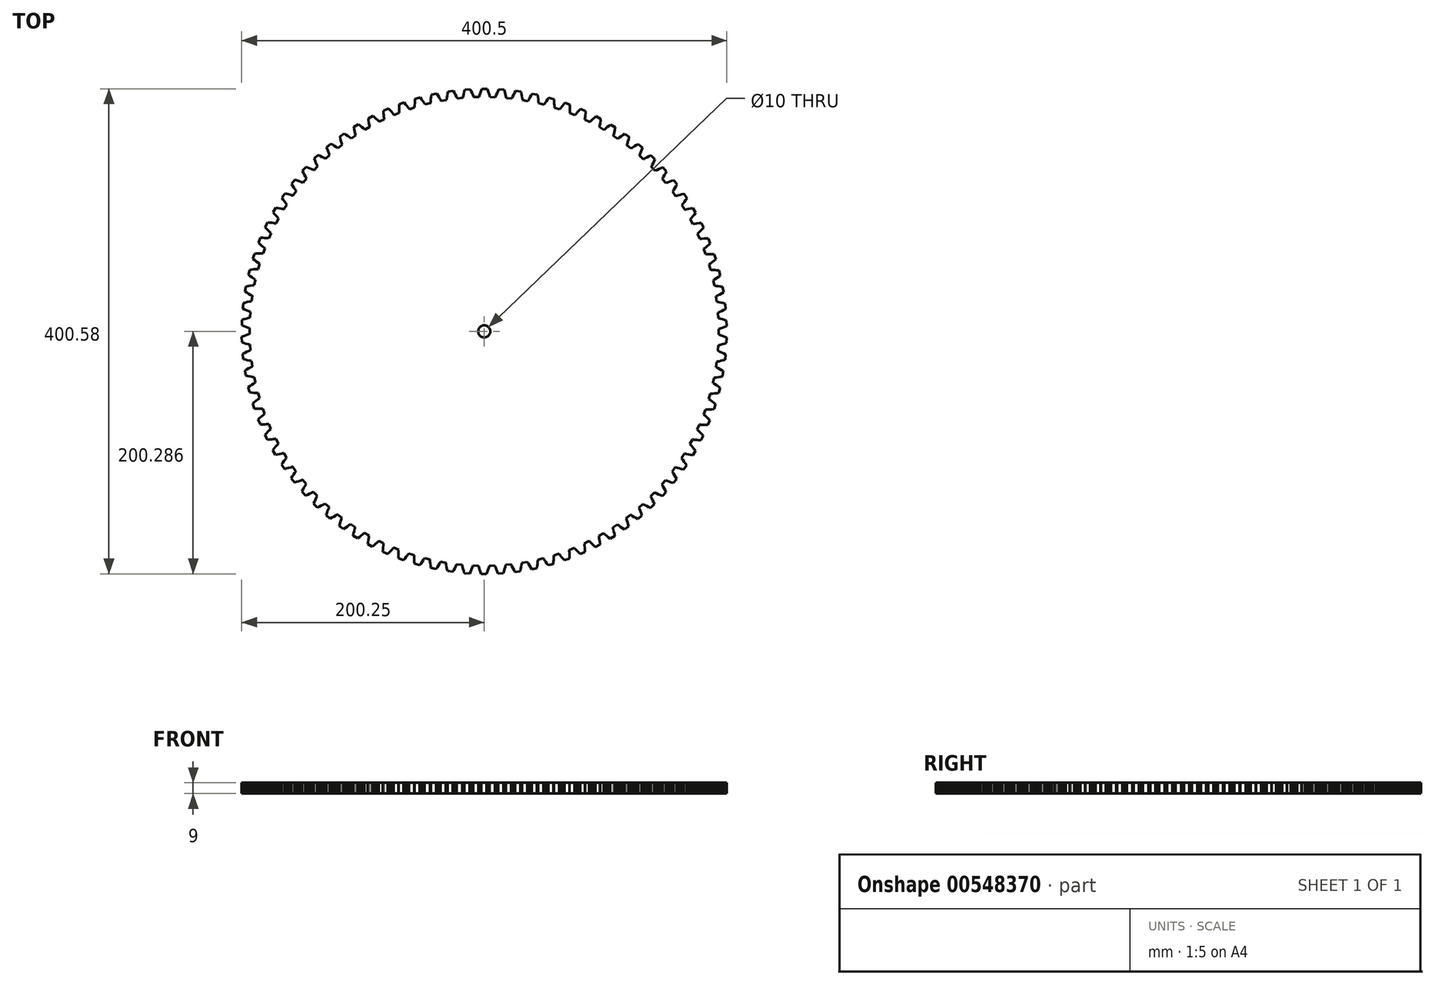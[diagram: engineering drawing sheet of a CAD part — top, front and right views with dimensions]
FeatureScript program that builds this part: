
annotation { "Feature Type Name" : "Feature", "Feature Type Description" : "" }
export const myFeature = defineFeature(function(context is Context, id is Id, definition is map)
    precondition{}
    {
        {
            var Q0;
            Q0=qCreatedBy(makeId("Top.planeOp"),FACE);
            var sketch = newSketch(context, id + "F0", { "sketchPlane" : qUnion([Q0])});
            skLineSegment(sketch, "E0.0.0", {"start": v(83.63, 88.8) * mm, "end": v(83.62, 84.25) * mm});
            skLineSegment(sketch, "E0.0.1", {"start": v(83.62, 84.25) * mm, "end": v(84.03, 84.11) * mm});
            skLineSegment(sketch, "E0.0.2", {"start": v(84.03, 84.11) * mm, "end": v(84.44, 83.97) * mm});
            skLineSegment(sketch, "E0.0.3", {"start": v(84.44, 83.97) * mm, "end": v(85.27, 83.69) * mm});
            skLineSegment(sketch, "E0.0.4", {"start": v(85.27, 83.69) * mm, "end": v(86.9, 83.08) * mm});
            skLineSegment(sketch, "E0.0.5", {"start": v(86.9, 83.08) * mm, "end": v(88.54, 82.43) * mm});
            skLineSegment(sketch, "E0.0.6", {"start": v(88.54, 82.43) * mm, "end": v(90.18, 81.73) * mm});
            skLineSegment(sketch, "E0.0.7", {"start": v(90.18, 81.73) * mm, "end": v(90.02, 77.33) * mm});
            skLineSegment(sketch, "E0.0.8", {"start": v(90.02, 77.33) * mm, "end": v(88.34, 76.75) * mm});
            skLineSegment(sketch, "E0.0.9", {"start": v(88.34, 76.75) * mm, "end": v(86.66, 76.21) * mm});
            skLineSegment(sketch, "E0.0.10", {"start": v(86.66, 76.21) * mm, "end": v(84.98, 75.72) * mm});
            skLineSegment(sketch, "E0.0.11", {"start": v(84.98, 75.72) * mm, "end": v(84.14, 75.5) * mm});
            skLineSegment(sketch, "E0.0.12", {"start": v(84.14, 75.5) * mm, "end": v(83.72, 75.4) * mm});
            skLineSegment(sketch, "E0.0.13", {"start": v(83.72, 75.4) * mm, "end": v(83.3, 75.29) * mm});
            skLineSegment(sketch, "E0.0.14", {"start": v(83.3, 75.29) * mm, "end": v(82.97, 70.74) * mm});
            skLineSegment(sketch, "E0.0.15", {"start": v(82.97, 70.74) * mm, "end": v(83.37, 70.58) * mm});
            skLineSegment(sketch, "E0.0.16", {"start": v(83.37, 70.58) * mm, "end": v(83.77, 70.41) * mm});
            skLineSegment(sketch, "E0.0.17", {"start": v(83.77, 70.41) * mm, "end": v(84.57, 70.07) * mm});
            skLineSegment(sketch, "E0.0.18", {"start": v(84.57, 70.07) * mm, "end": v(86.17, 69.35) * mm});
            skLineSegment(sketch, "E0.0.19", {"start": v(86.17, 69.35) * mm, "end": v(87.75, 68.58) * mm});
            skLineSegment(sketch, "E0.0.20", {"start": v(87.75, 68.58) * mm, "end": v(89.33, 67.77) * mm});
            skLineSegment(sketch, "E0.0.21", {"start": v(89.33, 67.77) * mm, "end": v(88.87, 63.4) * mm});
            skLineSegment(sketch, "E0.0.22", {"start": v(88.87, 63.4) * mm, "end": v(87.15, 62.93) * mm});
            skLineSegment(sketch, "E0.0.23", {"start": v(87.15, 62.93) * mm, "end": v(85.44, 62.51) * mm});
            skLineSegment(sketch, "E0.0.24", {"start": v(85.44, 62.51) * mm, "end": v(83.73, 62.15) * mm});
            skLineSegment(sketch, "E0.0.25", {"start": v(83.73, 62.15) * mm, "end": v(82.88, 61.98) * mm});
            skLineSegment(sketch, "E0.0.26", {"start": v(82.88, 61.98) * mm, "end": v(82.45, 61.9) * mm});
            skLineSegment(sketch, "E0.0.27", {"start": v(82.45, 61.9) * mm, "end": v(82.02, 61.83) * mm});
            skLineSegment(sketch, "E0.0.28", {"start": v(82.02, 61.83) * mm, "end": v(81.38, 57.31) * mm});
            skLineSegment(sketch, "E0.0.29", {"start": v(81.38, 57.31) * mm, "end": v(81.77, 57.12) * mm});
            skLineSegment(sketch, "E0.0.30", {"start": v(81.77, 57.12) * mm, "end": v(82.16, 56.93) * mm});
            skLineSegment(sketch, "E0.0.31", {"start": v(82.16, 56.93) * mm, "end": v(82.93, 56.54) * mm});
            skLineSegment(sketch, "E0.0.32", {"start": v(82.93, 56.54) * mm, "end": v(84.47, 55.7) * mm});
            skLineSegment(sketch, "E0.0.33", {"start": v(84.47, 55.7) * mm, "end": v(86, 54.83) * mm});
            skLineSegment(sketch, "E0.0.34", {"start": v(86, 54.83) * mm, "end": v(87.52, 53.9) * mm});
            skLineSegment(sketch, "E0.0.35", {"start": v(87.52, 53.9) * mm, "end": v(86.75, 49.57) * mm});
            skLineSegment(sketch, "E0.0.36", {"start": v(86.75, 49.57) * mm, "end": v(85, 49.23) * mm});
            skLineSegment(sketch, "E0.0.37", {"start": v(85, 49.23) * mm, "end": v(83.27, 48.94) * mm});
            skLineSegment(sketch, "E0.0.38", {"start": v(83.27, 48.94) * mm, "end": v(81.54, 48.69) * mm});
            skLineSegment(sketch, "E0.0.39", {"start": v(81.54, 48.69) * mm, "end": v(80.68, 48.58) * mm});
            skLineSegment(sketch, "E0.0.40", {"start": v(80.68, 48.58) * mm, "end": v(80.24, 48.53) * mm});
            skLineSegment(sketch, "E0.0.41", {"start": v(80.24, 48.53) * mm, "end": v(79.82, 48.5) * mm});
            skLineSegment(sketch, "E0.0.42", {"start": v(79.82, 48.5) * mm, "end": v(78.86, 44.03) * mm});
            skLineSegment(sketch, "E0.0.43", {"start": v(78.86, 44.03) * mm, "end": v(79.23, 43.82) * mm});
            skLineSegment(sketch, "E0.0.44", {"start": v(79.23, 43.82) * mm, "end": v(79.6, 43.6) * mm});
            skLineSegment(sketch, "E0.0.45", {"start": v(79.6, 43.6) * mm, "end": v(80.35, 43.15) * mm});
            skLineSegment(sketch, "E0.0.46", {"start": v(80.35, 43.15) * mm, "end": v(81.83, 42.21) * mm});
            skLineSegment(sketch, "E0.0.47", {"start": v(81.83, 42.21) * mm, "end": v(83.3, 41.23) * mm});
            skLineSegment(sketch, "E0.0.48", {"start": v(83.3, 41.23) * mm, "end": v(84.75, 40.2) * mm});
            skLineSegment(sketch, "E0.0.49", {"start": v(84.75, 40.2) * mm, "end": v(83.67, 35.93) * mm});
            skLineSegment(sketch, "E0.0.50", {"start": v(83.67, 35.93) * mm, "end": v(81.91, 35.72) * mm});
            skLineSegment(sketch, "E0.0.51", {"start": v(81.91, 35.72) * mm, "end": v(80.16, 35.54) * mm});
            skLineSegment(sketch, "E0.0.52", {"start": v(80.16, 35.54) * mm, "end": v(78.41, 35.42) * mm});
            skLineSegment(sketch, "E0.0.53", {"start": v(78.41, 35.42) * mm, "end": v(77.54, 35.37) * mm});
            skLineSegment(sketch, "E0.0.54", {"start": v(77.54, 35.37) * mm, "end": v(77.11, 35.35) * mm});
            skLineSegment(sketch, "E0.0.55", {"start": v(77.11, 35.35) * mm, "end": v(76.68, 35.34) * mm});
            skLineSegment(sketch, "E0.0.56", {"start": v(76.68, 35.34) * mm, "end": v(75.42, 30.96) * mm});
            skLineSegment(sketch, "E0.0.57", {"start": v(75.42, 30.96) * mm, "end": v(75.78, 30.72) * mm});
            skLineSegment(sketch, "E0.0.58", {"start": v(75.78, 30.72) * mm, "end": v(76.13, 30.47) * mm});
            skLineSegment(sketch, "E0.0.59", {"start": v(76.13, 30.47) * mm, "end": v(76.84, 29.97) * mm});
            skLineSegment(sketch, "E0.0.60", {"start": v(76.84, 29.97) * mm, "end": v(78.25, 28.94) * mm});
            skLineSegment(sketch, "E0.0.61", {"start": v(78.25, 28.94) * mm, "end": v(79.64, 27.85) * mm});
            skLineSegment(sketch, "E0.0.62", {"start": v(79.64, 27.85) * mm, "end": v(81.02, 26.73) * mm});
            skLineSegment(sketch, "E0.0.63", {"start": v(81.02, 26.73) * mm, "end": v(79.65, 22.54) * mm});
            skLineSegment(sketch, "E0.0.64", {"start": v(79.65, 22.54) * mm, "end": v(77.88, 22.45) * mm});
            skLineSegment(sketch, "E0.0.65", {"start": v(77.88, 22.45) * mm, "end": v(76.12, 22.4) * mm});
            skLineSegment(sketch, "E0.0.66", {"start": v(76.12, 22.4) * mm, "end": v(74.37, 22.4) * mm});
            skLineSegment(sketch, "E0.0.67", {"start": v(74.37, 22.4) * mm, "end": v(73.5, 22.4) * mm});
            skLineSegment(sketch, "E0.0.68", {"start": v(73.5, 22.4) * mm, "end": v(73.07, 22.42) * mm});
            skLineSegment(sketch, "E0.0.69", {"start": v(73.07, 22.42) * mm, "end": v(72.64, 22.44) * mm});
            skLineSegment(sketch, "E0.0.70", {"start": v(72.64, 22.44) * mm, "end": v(71.07, 18.16) * mm});
            skLineSegment(sketch, "E0.0.71", {"start": v(71.07, 18.16) * mm, "end": v(71.41, 17.89) * mm});
            skLineSegment(sketch, "E0.0.72", {"start": v(71.41, 17.89) * mm, "end": v(71.75, 17.62) * mm});
            skLineSegment(sketch, "E0.0.73", {"start": v(71.75, 17.62) * mm, "end": v(72.42, 17.07) * mm});
            skLineSegment(sketch, "E0.0.74", {"start": v(72.42, 17.07) * mm, "end": v(73.76, 15.94) * mm});
            skLineSegment(sketch, "E0.0.75", {"start": v(73.76, 15.94) * mm, "end": v(75.07, 14.77) * mm});
            skLineSegment(sketch, "E0.0.76", {"start": v(75.07, 14.77) * mm, "end": v(76.37, 13.55) * mm});
            skLineSegment(sketch, "E0.0.77", {"start": v(76.37, 13.55) * mm, "end": v(74.71, 9.47) * mm});
            skLineSegment(sketch, "E0.0.78", {"start": v(74.71, 9.47) * mm, "end": v(72.93, 9.5) * mm});
            skLineSegment(sketch, "E0.0.79", {"start": v(72.93, 9.5) * mm, "end": v(71.17, 9.57) * mm});
            skLineSegment(sketch, "E0.0.80", {"start": v(71.17, 9.57) * mm, "end": v(69.43, 9.69) * mm});
            skLineSegment(sketch, "E0.0.81", {"start": v(69.43, 9.69) * mm, "end": v(68.56, 9.76) * mm});
            skLineSegment(sketch, "E0.0.82", {"start": v(68.56, 9.76) * mm, "end": v(68.13, 9.8) * mm});
            skLineSegment(sketch, "E0.0.83", {"start": v(68.13, 9.8) * mm, "end": v(67.7, 9.85) * mm});
            skLineSegment(sketch, "E0.0.84", {"start": v(67.7, 9.85) * mm, "end": v(65.84, 5.69) * mm});
            skLineSegment(sketch, "E0.0.85", {"start": v(65.84, 5.69) * mm, "end": v(66.16, 5.4) * mm});
            skLineSegment(sketch, "E0.0.86", {"start": v(66.16, 5.4) * mm, "end": v(66.48, 5.1) * mm});
            skLineSegment(sketch, "E0.0.87", {"start": v(66.48, 5.1) * mm, "end": v(67.12, 4.51) * mm});
            skLineSegment(sketch, "E0.0.88", {"start": v(67.12, 4.51) * mm, "end": v(68.37, 3.3) * mm});
            skLineSegment(sketch, "E0.0.89", {"start": v(68.37, 3.3) * mm, "end": v(69.6, 2.03) * mm});
            skLineSegment(sketch, "E0.0.90", {"start": v(69.6, 2.03) * mm, "end": v(70.8, 0.72) * mm});
            skLineSegment(sketch, "E0.0.91", {"start": v(70.8, 0.72) * mm, "end": v(68.87, -3.23) * mm});
            skLineSegment(sketch, "E0.0.92", {"start": v(68.87, -3.23) * mm, "end": v(67.1, -3.08) * mm});
            skLineSegment(sketch, "E0.0.93", {"start": v(67.1, -3.08) * mm, "end": v(65.34, -2.89) * mm});
            skLineSegment(sketch, "E0.0.94", {"start": v(65.34, -2.89) * mm, "end": v(63.61, -2.65) * mm});
            skLineSegment(sketch, "E0.0.95", {"start": v(63.61, -2.65) * mm, "end": v(62.75, -2.51) * mm});
            skLineSegment(sketch, "E0.0.96", {"start": v(62.75, -2.51) * mm, "end": v(62.33, -2.44) * mm});
            skLineSegment(sketch, "E0.0.97", {"start": v(62.33, -2.44) * mm, "end": v(61.9, -2.36) * mm});
            skLineSegment(sketch, "E0.0.98", {"start": v(61.9, -2.36) * mm, "end": v(59.76, -6.38) * mm});
            skLineSegment(sketch, "E0.0.99", {"start": v(59.76, -6.38) * mm, "end": v(60.06, -6.7) * mm});
            skLineSegment(sketch, "E0.0.100", {"start": v(60.06, -6.7) * mm, "end": v(60.35, -7.01) * mm});
            skLineSegment(sketch, "E0.0.101", {"start": v(60.35, -7.01) * mm, "end": v(60.94, -7.65) * mm});
            skLineSegment(sketch, "E0.0.102", {"start": v(60.94, -7.65) * mm, "end": v(62.1, -8.95) * mm});
            skLineSegment(sketch, "E0.0.103", {"start": v(62.1, -8.95) * mm, "end": v(63.24, -10.3) * mm});
            skLineSegment(sketch, "E0.0.104", {"start": v(63.24, -10.3) * mm, "end": v(64.36, -11.68) * mm});
            skLineSegment(sketch, "E0.0.105", {"start": v(64.36, -11.68) * mm, "end": v(62.15, -15.5) * mm});
            skLineSegment(sketch, "E0.0.106", {"start": v(62.15, -15.5) * mm, "end": v(60.4, -15.22) * mm});
            skLineSegment(sketch, "E0.0.107", {"start": v(60.4, -15.22) * mm, "end": v(58.66, -14.9) * mm});
            skLineSegment(sketch, "E0.0.108", {"start": v(58.66, -14.9) * mm, "end": v(56.95, -14.54) * mm});
            skLineSegment(sketch, "E0.0.109", {"start": v(56.95, -14.54) * mm, "end": v(56.1, -14.35) * mm});
            skLineSegment(sketch, "E0.0.110", {"start": v(56.1, -14.35) * mm, "end": v(55.68, -14.25) * mm});
            skLineSegment(sketch, "E0.0.111", {"start": v(55.68, -14.25) * mm, "end": v(55.26, -14.14) * mm});
            skLineSegment(sketch, "E0.0.112", {"start": v(55.26, -14.14) * mm, "end": v(52.84, -18) * mm});
            skLineSegment(sketch, "E0.0.113", {"start": v(52.84, -18) * mm, "end": v(53.12, -18.34) * mm});
            skLineSegment(sketch, "E0.0.114", {"start": v(53.12, -18.34) * mm, "end": v(53.4, -18.67) * mm});
            skLineSegment(sketch, "E0.0.115", {"start": v(53.4, -18.67) * mm, "end": v(53.94, -19.35) * mm});
            skLineSegment(sketch, "E0.0.116", {"start": v(53.94, -19.35) * mm, "end": v(55, -20.73) * mm});
            skLineSegment(sketch, "E0.0.117", {"start": v(55, -20.73) * mm, "end": v(56.05, -22.15) * mm});
            skLineSegment(sketch, "E0.0.118", {"start": v(56.05, -22.15) * mm, "end": v(57.06, -23.61) * mm});
            skLineSegment(sketch, "E0.0.119", {"start": v(57.06, -23.61) * mm, "end": v(54.6, -27.26) * mm});
            skLineSegment(sketch, "E0.0.120", {"start": v(54.6, -27.26) * mm, "end": v(52.86, -26.86) * mm});
            skLineSegment(sketch, "E0.0.121", {"start": v(52.86, -26.86) * mm, "end": v(51.15, -26.42) * mm});
            skLineSegment(sketch, "E0.0.122", {"start": v(51.15, -26.42) * mm, "end": v(49.47, -25.95) * mm});
            skLineSegment(sketch, "E0.0.123", {"start": v(49.47, -25.95) * mm, "end": v(48.64, -25.7) * mm});
            skLineSegment(sketch, "E0.0.124", {"start": v(48.64, -25.7) * mm, "end": v(48.23, -25.56) * mm});
            skLineSegment(sketch, "E0.0.125", {"start": v(48.23, -25.56) * mm, "end": v(47.82, -25.43) * mm});
            skLineSegment(sketch, "E0.0.126", {"start": v(47.82, -25.43) * mm, "end": v(45.13, -29.11) * mm});
            skLineSegment(sketch, "E0.0.127", {"start": v(45.13, -29.11) * mm, "end": v(45.39, -29.46) * mm});
            skLineSegment(sketch, "E0.0.128", {"start": v(45.39, -29.46) * mm, "end": v(45.64, -29.81) * mm});
            skLineSegment(sketch, "E0.0.129", {"start": v(45.64, -29.81) * mm, "end": v(46.14, -30.53) * mm});
            skLineSegment(sketch, "E0.0.130", {"start": v(46.14, -30.53) * mm, "end": v(47.1, -31.98) * mm});
            skLineSegment(sketch, "E0.0.131", {"start": v(47.1, -31.98) * mm, "end": v(48.04, -33.47) * mm});
            skLineSegment(sketch, "E0.0.132", {"start": v(48.04, -33.47) * mm, "end": v(48.95, -35) * mm});
            skLineSegment(sketch, "E0.0.133", {"start": v(48.95, -35) * mm, "end": v(46.24, -38.47) * mm});
            skLineSegment(sketch, "E0.0.134", {"start": v(46.24, -38.47) * mm, "end": v(44.54, -37.95) * mm});
            skLineSegment(sketch, "E0.0.135", {"start": v(44.54, -37.95) * mm, "end": v(42.86, -37.4) * mm});
            skLineSegment(sketch, "E0.0.136", {"start": v(42.86, -37.4) * mm, "end": v(41.22, -36.8) * mm});
            skLineSegment(sketch, "E0.0.137", {"start": v(41.22, -36.8) * mm, "end": v(40.4, -36.49) * mm});
            skLineSegment(sketch, "E0.0.138", {"start": v(40.4, -36.49) * mm, "end": v(40, -36.33) * mm});
            skLineSegment(sketch, "E0.0.139", {"start": v(40, -36.33) * mm, "end": v(39.6, -36.17) * mm});
            skLineSegment(sketch, "E0.0.140", {"start": v(39.6, -36.17) * mm, "end": v(36.67, -39.66) * mm});
            skLineSegment(sketch, "E0.0.141", {"start": v(36.67, -39.66) * mm, "end": v(36.9, -40.02) * mm});
            skLineSegment(sketch, "E0.0.142", {"start": v(36.9, -40.02) * mm, "end": v(37.13, -40.4) * mm});
            skLineSegment(sketch, "E0.0.143", {"start": v(37.13, -40.4) * mm, "end": v(37.57, -41.14) * mm});
            skLineSegment(sketch, "E0.0.144", {"start": v(37.57, -41.14) * mm, "end": v(38.44, -42.66) * mm});
            skLineSegment(sketch, "E0.0.145", {"start": v(38.44, -42.66) * mm, "end": v(39.27, -44.2) * mm});
            skLineSegment(sketch, "E0.0.146", {"start": v(39.27, -44.2) * mm, "end": v(40.07, -45.8) * mm});
            skLineSegment(sketch, "E0.0.147", {"start": v(40.07, -45.8) * mm, "end": v(37.12, -49.06) * mm});
            skLineSegment(sketch, "E0.0.148", {"start": v(37.12, -49.06) * mm, "end": v(35.46, -48.43) * mm});
            skLineSegment(sketch, "E0.0.149", {"start": v(35.46, -48.43) * mm, "end": v(33.83, -47.76) * mm});
            skLineSegment(sketch, "E0.0.150", {"start": v(33.83, -47.76) * mm, "end": v(32.23, -47.05) * mm});
            skLineSegment(sketch, "E0.0.151", {"start": v(32.23, -47.05) * mm, "end": v(31.44, -46.69) * mm});
            skLineSegment(sketch, "E0.0.152", {"start": v(31.44, -46.69) * mm, "end": v(31.05, -46.5) * mm});
            skLineSegment(sketch, "E0.0.153", {"start": v(31.05, -46.5) * mm, "end": v(30.66, -46.3) * mm});
            skLineSegment(sketch, "E0.0.154", {"start": v(30.66, -46.3) * mm, "end": v(27.5, -49.58) * mm});
            skLineSegment(sketch, "E0.0.155", {"start": v(27.5, -49.58) * mm, "end": v(27.7, -49.96) * mm});
            skLineSegment(sketch, "E0.0.156", {"start": v(27.7, -49.96) * mm, "end": v(27.9, -50.35) * mm});
            skLineSegment(sketch, "E0.0.157", {"start": v(27.9, -50.35) * mm, "end": v(28.29, -51.12) * mm});
            skLineSegment(sketch, "E0.0.158", {"start": v(28.29, -51.12) * mm, "end": v(29.05, -52.7) * mm});
            skLineSegment(sketch, "E0.0.159", {"start": v(29.05, -52.7) * mm, "end": v(29.77, -54.3) * mm});
            skLineSegment(sketch, "E0.0.160", {"start": v(29.77, -54.3) * mm, "end": v(30.46, -55.95) * mm});
            skLineSegment(sketch, "E0.0.161", {"start": v(30.46, -55.95) * mm, "end": v(27.28, -59) * mm});
            skLineSegment(sketch, "E0.0.162", {"start": v(27.28, -59) * mm, "end": v(25.67, -58.25) * mm});
            skLineSegment(sketch, "E0.0.163", {"start": v(25.67, -58.25) * mm, "end": v(24.1, -57.47) * mm});
            skLineSegment(sketch, "E0.0.164", {"start": v(24.1, -57.47) * mm, "end": v(22.55, -56.65) * mm});
            skLineSegment(sketch, "E0.0.165", {"start": v(22.55, -56.65) * mm, "end": v(21.79, -56.23) * mm});
            skLineSegment(sketch, "E0.0.166", {"start": v(21.79, -56.23) * mm, "end": v(21.41, -56.02) * mm});
            skLineSegment(sketch, "E0.0.167", {"start": v(21.41, -56.02) * mm, "end": v(21.04, -55.8) * mm});
            skLineSegment(sketch, "E0.0.168", {"start": v(21.04, -55.8) * mm, "end": v(17.64, -58.85) * mm});
            skLineSegment(sketch, "E0.0.169", {"start": v(17.64, -58.85) * mm, "end": v(17.82, -59.24) * mm});
            skLineSegment(sketch, "E0.0.170", {"start": v(17.82, -59.24) * mm, "end": v(18, -59.64) * mm});
            skLineSegment(sketch, "E0.0.171", {"start": v(18, -59.64) * mm, "end": v(18.33, -60.44) * mm});
            skLineSegment(sketch, "E0.0.172", {"start": v(18.33, -60.44) * mm, "end": v(18.98, -62.06) * mm});
            skLineSegment(sketch, "E0.0.173", {"start": v(18.98, -62.06) * mm, "end": v(19.58, -63.72) * mm});
            skLineSegment(sketch, "E0.0.174", {"start": v(19.58, -63.72) * mm, "end": v(20.16, -65.4) * mm});
            skLineSegment(sketch, "E0.0.175", {"start": v(20.16, -65.4) * mm, "end": v(16.78, -68.23) * mm});
            skLineSegment(sketch, "E0.0.176", {"start": v(16.78, -68.23) * mm, "end": v(15.22, -67.37) * mm});
            skLineSegment(sketch, "E0.0.177", {"start": v(15.22, -67.37) * mm, "end": v(13.7, -66.48) * mm});
            skLineSegment(sketch, "E0.0.178", {"start": v(13.7, -66.48) * mm, "end": v(12.22, -65.55) * mm});
            skLineSegment(sketch, "E0.0.179", {"start": v(12.22, -65.55) * mm, "end": v(11.49, -65.08) * mm});
            skLineSegment(sketch, "E0.0.180", {"start": v(11.49, -65.08) * mm, "end": v(11.13, -64.84) * mm});
            skLineSegment(sketch, "E0.0.181", {"start": v(11.13, -64.84) * mm, "end": v(10.77, -64.6) * mm});
            skLineSegment(sketch, "E0.0.182", {"start": v(10.77, -64.6) * mm, "end": v(7.17, -67.4) * mm});
            skLineSegment(sketch, "E0.0.183", {"start": v(7.17, -67.4) * mm, "end": v(7.32, -67.8) * mm});
            skLineSegment(sketch, "E0.0.184", {"start": v(7.32, -67.8) * mm, "end": v(7.47, -68.21) * mm});
            skLineSegment(sketch, "E0.0.185", {"start": v(7.47, -68.21) * mm, "end": v(7.75, -69.04) * mm});
            skLineSegment(sketch, "E0.0.186", {"start": v(7.75, -69.04) * mm, "end": v(8.28, -70.7) * mm});
            skLineSegment(sketch, "E0.0.187", {"start": v(8.28, -70.7) * mm, "end": v(8.77, -72.4) * mm});
            skLineSegment(sketch, "E0.0.188", {"start": v(8.77, -72.4) * mm, "end": v(9.22, -74.11) * mm});
            skLineSegment(sketch, "E0.0.189", {"start": v(9.22, -74.11) * mm, "end": v(5.66, -76.7) * mm});
            skLineSegment(sketch, "E0.0.190", {"start": v(5.66, -76.7) * mm, "end": v(4.16, -75.73) * mm});
            skLineSegment(sketch, "E0.0.191", {"start": v(4.16, -75.73) * mm, "end": v(2.7, -74.74) * mm});
            skLineSegment(sketch, "E0.0.192", {"start": v(2.7, -74.74) * mm, "end": v(1.3, -73.71) * mm});
            skLineSegment(sketch, "E0.0.193", {"start": v(1.3, -73.71) * mm, "end": v(0.6, -73.19) * mm});
            skLineSegment(sketch, "E0.0.194", {"start": v(0.6, -73.19) * mm, "end": v(0.26, -72.92) * mm});
            skLineSegment(sketch, "E0.0.195", {"start": v(0.26, -72.92) * mm, "end": v(-0.08, -72.66) * mm});
            skLineSegment(sketch, "E0.0.196", {"start": v(-0.08, -72.66) * mm, "end": v(-3.87, -75.2) * mm});
            skLineSegment(sketch, "E0.0.197", {"start": v(-3.87, -75.2) * mm, "end": v(-3.75, -75.62) * mm});
            skLineSegment(sketch, "E0.0.198", {"start": v(-3.75, -75.62) * mm, "end": v(-3.63, -76.03) * mm});
            skLineSegment(sketch, "E0.0.199", {"start": v(-3.63, -76.03) * mm, "end": v(-3.41, -76.87) * mm});
            skLineSegment(sketch, "E0.0.200", {"start": v(-3.41, -76.87) * mm, "end": v(-3, -78.57) * mm});
            skLineSegment(sketch, "E0.0.201", {"start": v(-3, -78.57) * mm, "end": v(-2.62, -80.3) * mm});
            skLineSegment(sketch, "E0.0.202", {"start": v(-2.62, -80.3) * mm, "end": v(-2.3, -82.04) * mm});
            skLineSegment(sketch, "E0.0.203", {"start": v(-2.3, -82.04) * mm, "end": v(-6.03, -84.37) * mm});
            skLineSegment(sketch, "E0.0.204", {"start": v(-6.03, -84.37) * mm, "end": v(-7.45, -83.3) * mm});
            skLineSegment(sketch, "E0.0.205", {"start": v(-7.45, -83.3) * mm, "end": v(-8.83, -82.2) * mm});
            skLineSegment(sketch, "E0.0.206", {"start": v(-8.83, -82.2) * mm, "end": v(-10.18, -81.09) * mm});
            skLineSegment(sketch, "E0.0.207", {"start": v(-10.18, -81.09) * mm, "end": v(-10.83, -80.52) * mm});
            skLineSegment(sketch, "E0.0.208", {"start": v(-10.83, -80.52) * mm, "end": v(-11.15, -80.23) * mm});
            skLineSegment(sketch, "E0.0.209", {"start": v(-11.15, -80.23) * mm, "end": v(-11.48, -79.94) * mm});
            skLineSegment(sketch, "E0.0.210", {"start": v(-11.48, -79.94) * mm, "end": v(-15.43, -82.21) * mm});
            skLineSegment(sketch, "E0.0.211", {"start": v(-15.43, -82.21) * mm, "end": v(-15.34, -82.64) * mm});
            skLineSegment(sketch, "E0.0.212", {"start": v(-15.34, -82.64) * mm, "end": v(-15.25, -83.06) * mm});
            skLineSegment(sketch, "E0.0.213", {"start": v(-15.25, -83.06) * mm, "end": v(-15.09, -83.91) * mm});
            skLineSegment(sketch, "E0.0.214", {"start": v(-15.09, -83.91) * mm, "end": v(-14.8, -85.64) * mm});
            skLineSegment(sketch, "E0.0.215", {"start": v(-14.8, -85.64) * mm, "end": v(-14.54, -87.38) * mm});
            skLineSegment(sketch, "E0.0.216", {"start": v(-14.54, -87.38) * mm, "end": v(-14.33, -89.15) * mm});
            skLineSegment(sketch, "E0.0.217", {"start": v(-14.33, -89.15) * mm, "end": v(-18.22, -91.2) * mm});
            skLineSegment(sketch, "E0.0.218", {"start": v(-18.22, -91.2) * mm, "end": v(-19.57, -90.04) * mm});
            skLineSegment(sketch, "E0.0.219", {"start": v(-19.57, -90.04) * mm, "end": v(-20.87, -88.86) * mm});
            skLineSegment(sketch, "E0.0.220", {"start": v(-20.87, -88.86) * mm, "end": v(-22.13, -87.65) * mm});
            skLineSegment(sketch, "E0.0.221", {"start": v(-22.13, -87.65) * mm, "end": v(-22.74, -87.03) * mm});
            skLineSegment(sketch, "E0.0.222", {"start": v(-22.74, -87.03) * mm, "end": v(-23.05, -86.72) * mm});
            skLineSegment(sketch, "E0.0.223", {"start": v(-23.05, -86.72) * mm, "end": v(-23.35, -86.41) * mm});
            skLineSegment(sketch, "E0.0.224", {"start": v(-23.35, -86.41) * mm, "end": v(-27.45, -88.4) * mm});
            skLineSegment(sketch, "E0.0.225", {"start": v(-27.45, -88.4) * mm, "end": v(-27.39, -88.83) * mm});
            skLineSegment(sketch, "E0.0.226", {"start": v(-27.39, -88.83) * mm, "end": v(-27.33, -89.26) * mm});
            skLineSegment(sketch, "E0.0.227", {"start": v(-27.33, -89.26) * mm, "end": v(-27.23, -90.12) * mm});
            skLineSegment(sketch, "E0.0.228", {"start": v(-27.23, -90.12) * mm, "end": v(-27.05, -91.86) * mm});
            skLineSegment(sketch, "E0.0.229", {"start": v(-27.05, -91.86) * mm, "end": v(-26.92, -93.62) * mm});
            skLineSegment(sketch, "E0.0.230", {"start": v(-26.92, -93.62) * mm, "end": v(-26.84, -95.4) * mm});
            skLineSegment(sketch, "E0.0.231", {"start": v(-26.84, -95.4) * mm, "end": v(-30.86, -97.18) * mm});
            skLineSegment(sketch, "E0.0.232", {"start": v(-30.86, -97.18) * mm, "end": v(-32.12, -95.93) * mm});
            skLineSegment(sketch, "E0.0.233", {"start": v(-32.12, -95.93) * mm, "end": v(-33.34, -94.65) * mm});
            skLineSegment(sketch, "E0.0.234", {"start": v(-33.34, -94.65) * mm, "end": v(-34.51, -93.36) * mm});
            skLineSegment(sketch, "E0.0.235", {"start": v(-34.51, -93.36) * mm, "end": v(-35.08, -92.7) * mm});
            skLineSegment(sketch, "E0.0.236", {"start": v(-35.08, -92.7) * mm, "end": v(-35.36, -92.37) * mm});
            skLineSegment(sketch, "E0.0.237", {"start": v(-35.36, -92.37) * mm, "end": v(-35.64, -92.04) * mm});
            skLineSegment(sketch, "E0.0.238", {"start": v(-35.64, -92.04) * mm, "end": v(-39.87, -93.74) * mm});
            skLineSegment(sketch, "E0.0.239", {"start": v(-39.87, -93.74) * mm, "end": v(-39.84, -94.17) * mm});
            skLineSegment(sketch, "E0.0.240", {"start": v(-39.84, -94.17) * mm, "end": v(-39.81, -94.6) * mm});
            skLineSegment(sketch, "E0.0.241", {"start": v(-39.81, -94.6) * mm, "end": v(-39.77, -95.47) * mm});
            skLineSegment(sketch, "E0.0.242", {"start": v(-39.77, -95.47) * mm, "end": v(-39.72, -97.22) * mm});
            skLineSegment(sketch, "E0.0.243", {"start": v(-39.72, -97.22) * mm, "end": v(-39.71, -98.98) * mm});
            skLineSegment(sketch, "E0.0.244", {"start": v(-39.71, -98.98) * mm, "end": v(-39.75, -100.76) * mm});
            skLineSegment(sketch, "E0.0.245", {"start": v(-39.75, -100.76) * mm, "end": v(-43.9, -102.26) * mm});
            skLineSegment(sketch, "E0.0.246", {"start": v(-43.9, -102.26) * mm, "end": v(-45.06, -100.92) * mm});
            skLineSegment(sketch, "E0.0.247", {"start": v(-45.06, -100.92) * mm, "end": v(-46.18, -99.56) * mm});
            skLineSegment(sketch, "E0.0.248", {"start": v(-46.18, -99.56) * mm, "end": v(-47.26, -98.19) * mm});
            skLineSegment(sketch, "E0.0.249", {"start": v(-47.26, -98.19) * mm, "end": v(-47.79, -97.5) * mm});
            skLineSegment(sketch, "E0.0.250", {"start": v(-47.79, -97.5) * mm, "end": v(-48.04, -97.14) * mm});
            skLineSegment(sketch, "E0.0.251", {"start": v(-48.04, -97.14) * mm, "end": v(-48.3, -96.8) * mm});
            skLineSegment(sketch, "E0.0.252", {"start": v(-48.3, -96.8) * mm, "end": v(-52.63, -98.2) * mm});
            skLineSegment(sketch, "E0.0.253", {"start": v(-52.63, -98.2) * mm, "end": v(-52.63, -98.63) * mm});
            skLineSegment(sketch, "E0.0.254", {"start": v(-52.63, -98.63) * mm, "end": v(-52.64, -99.06) * mm});
            skLineSegment(sketch, "E0.0.255", {"start": v(-52.64, -99.06) * mm, "end": v(-52.66, -99.93) * mm});
            skLineSegment(sketch, "E0.0.256", {"start": v(-52.66, -99.93) * mm, "end": v(-52.73, -101.68) * mm});
            skLineSegment(sketch, "E0.0.257", {"start": v(-52.73, -101.68) * mm, "end": v(-52.84, -103.44) * mm});
            skLineSegment(sketch, "E0.0.258", {"start": v(-52.84, -103.44) * mm, "end": v(-53, -105.2) * mm});
            skLineSegment(sketch, "E0.0.259", {"start": v(-53, -105.2) * mm, "end": v(-57.24, -106.41) * mm});
            skLineSegment(sketch, "E0.0.260", {"start": v(-57.24, -106.41) * mm, "end": v(-58.31, -105) * mm});
            skLineSegment(sketch, "E0.0.261", {"start": v(-58.31, -105) * mm, "end": v(-59.34, -103.56) * mm});
            skLineSegment(sketch, "E0.0.262", {"start": v(-59.34, -103.56) * mm, "end": v(-60.32, -102.12) * mm});
            skLineSegment(sketch, "E0.0.263", {"start": v(-60.32, -102.12) * mm, "end": v(-60.8, -101.39) * mm});
            skLineSegment(sketch, "E0.0.264", {"start": v(-60.8, -101.39) * mm, "end": v(-61.02, -101.02) * mm});
            skLineSegment(sketch, "E0.0.265", {"start": v(-61.02, -101.02) * mm, "end": v(-61.25, -100.66) * mm});
            skLineSegment(sketch, "E0.0.266", {"start": v(-61.25, -100.66) * mm, "end": v(-65.68, -101.75) * mm});
            skLineSegment(sketch, "E0.0.267", {"start": v(-65.68, -101.75) * mm, "end": v(-65.7, -102.18) * mm});
            skLineSegment(sketch, "E0.0.268", {"start": v(-65.7, -102.18) * mm, "end": v(-65.74, -102.61) * mm});
            skLineSegment(sketch, "E0.0.269", {"start": v(-65.74, -102.61) * mm, "end": v(-65.82, -103.48) * mm});
            skLineSegment(sketch, "E0.0.270", {"start": v(-65.82, -103.48) * mm, "end": v(-66.01, -105.22) * mm});
            skLineSegment(sketch, "E0.0.271", {"start": v(-66.01, -105.22) * mm, "end": v(-66.25, -106.96) * mm});
            skLineSegment(sketch, "E0.0.272", {"start": v(-66.25, -106.96) * mm, "end": v(-66.54, -108.72) * mm});
            skLineSegment(sketch, "E0.0.273", {"start": v(-66.54, -108.72) * mm, "end": v(-70.85, -109.63) * mm});
            skLineSegment(sketch, "E0.0.274", {"start": v(-70.85, -109.63) * mm, "end": v(-71.82, -108.14) * mm});
            skLineSegment(sketch, "E0.0.275", {"start": v(-71.82, -108.14) * mm, "end": v(-72.74, -106.64) * mm});
            skLineSegment(sketch, "E0.0.276", {"start": v(-72.74, -106.64) * mm, "end": v(-73.62, -105.13) * mm});
            skLineSegment(sketch, "E0.0.277", {"start": v(-73.62, -105.13) * mm, "end": v(-74.04, -104.37) * mm});
            skLineSegment(sketch, "E0.0.278", {"start": v(-74.04, -104.37) * mm, "end": v(-74.25, -103.98) * mm});
            skLineSegment(sketch, "E0.0.279", {"start": v(-74.25, -103.98) * mm, "end": v(-74.45, -103.6) * mm});
            skLineSegment(sketch, "E0.0.280", {"start": v(-74.45, -103.6) * mm, "end": v(-78.94, -104.39) * mm});
            skLineSegment(sketch, "E0.0.281", {"start": v(-78.94, -104.39) * mm, "end": v(-79, -104.82) * mm});
            skLineSegment(sketch, "E0.0.282", {"start": v(-79, -104.82) * mm, "end": v(-79.06, -105.24) * mm});
            skLineSegment(sketch, "E0.0.283", {"start": v(-79.06, -105.24) * mm, "end": v(-79.2, -106.1) * mm});
            skLineSegment(sketch, "E0.0.284", {"start": v(-79.2, -106.1) * mm, "end": v(-79.51, -107.82) * mm});
            skLineSegment(sketch, "E0.0.285", {"start": v(-79.51, -107.82) * mm, "end": v(-79.88, -109.55) * mm});
            skLineSegment(sketch, "E0.0.286", {"start": v(-79.88, -109.55) * mm, "end": v(-80.28, -111.28) * mm});
            skLineSegment(sketch, "E0.0.287", {"start": v(-80.28, -111.28) * mm, "end": v(-84.64, -111.88) * mm});
            skLineSegment(sketch, "E0.0.288", {"start": v(-84.64, -111.88) * mm, "end": v(-85.5, -110.33) * mm});
            skLineSegment(sketch, "E0.0.289", {"start": v(-85.5, -110.33) * mm, "end": v(-86.32, -108.77) * mm});
            skLineSegment(sketch, "E0.0.290", {"start": v(-86.32, -108.77) * mm, "end": v(-87.1, -107.2) * mm});
            skLineSegment(sketch, "E0.0.291", {"start": v(-87.1, -107.2) * mm, "end": v(-87.46, -106.41) * mm});
            skLineSegment(sketch, "E0.0.292", {"start": v(-87.46, -106.41) * mm, "end": v(-87.64, -106.02) * mm});
            skLineSegment(sketch, "E0.0.293", {"start": v(-87.64, -106.02) * mm, "end": v(-87.82, -105.62) * mm});
            skLineSegment(sketch, "E0.0.294", {"start": v(-87.82, -105.62) * mm, "end": v(-92.35, -106.1) * mm});
            skLineSegment(sketch, "E0.0.295", {"start": v(-92.35, -106.1) * mm, "end": v(-92.44, -106.52) * mm});
            skLineSegment(sketch, "E0.0.296", {"start": v(-92.44, -106.52) * mm, "end": v(-92.53, -106.94) * mm});
            skLineSegment(sketch, "E0.0.297", {"start": v(-92.53, -106.94) * mm, "end": v(-92.73, -107.78) * mm});
            skLineSegment(sketch, "E0.0.298", {"start": v(-92.73, -107.78) * mm, "end": v(-93.16, -109.48) * mm});
            skLineSegment(sketch, "E0.0.299", {"start": v(-93.16, -109.48) * mm, "end": v(-93.64, -111.17) * mm});
            skLineSegment(sketch, "E0.0.300", {"start": v(-93.64, -111.17) * mm, "end": v(-94.17, -112.87) * mm});
            skLineSegment(sketch, "E0.0.301", {"start": v(-94.17, -112.87) * mm, "end": v(-98.56, -113.17) * mm});
            skLineSegment(sketch, "E0.0.302", {"start": v(-98.56, -113.17) * mm, "end": v(-99.32, -111.56) * mm});
            skLineSegment(sketch, "E0.0.303", {"start": v(-99.32, -111.56) * mm, "end": v(-100.02, -109.95) * mm});
            skLineSegment(sketch, "E0.0.304", {"start": v(-100.02, -109.95) * mm, "end": v(-100.68, -108.33) * mm});
            skLineSegment(sketch, "E0.0.305", {"start": v(-100.68, -108.33) * mm, "end": v(-101, -107.52) * mm});
            skLineSegment(sketch, "E0.0.306", {"start": v(-101, -107.52) * mm, "end": v(-101.15, -107.11) * mm});
            skLineSegment(sketch, "E0.0.307", {"start": v(-101.15, -107.11) * mm, "end": v(-101.3, -106.7) * mm});
            skLineSegment(sketch, "E0.0.308", {"start": v(-101.3, -106.7) * mm, "end": v(-105.85, -106.86) * mm});
            skLineSegment(sketch, "E0.0.309", {"start": v(-105.85, -106.86) * mm, "end": v(-105.97, -107.27) * mm});
            skLineSegment(sketch, "E0.0.310", {"start": v(-105.97, -107.27) * mm, "end": v(-106.1, -107.69) * mm});
            skLineSegment(sketch, "E0.0.311", {"start": v(-106.1, -107.69) * mm, "end": v(-106.35, -108.52) * mm});
            skLineSegment(sketch, "E0.0.312", {"start": v(-106.35, -108.52) * mm, "end": v(-106.9, -110.18) * mm});
            skLineSegment(sketch, "E0.0.313", {"start": v(-106.9, -110.18) * mm, "end": v(-107.5, -111.84) * mm});
            skLineSegment(sketch, "E0.0.314", {"start": v(-107.5, -111.84) * mm, "end": v(-108.14, -113.5) * mm});
            skLineSegment(sketch, "E0.0.315", {"start": v(-108.14, -113.5) * mm, "end": v(-112.54, -113.49) * mm});
            skLineSegment(sketch, "E0.0.316", {"start": v(-112.54, -113.49) * mm, "end": v(-113.18, -111.83) * mm});
            skLineSegment(sketch, "E0.0.317", {"start": v(-113.18, -111.83) * mm, "end": v(-113.77, -110.17) * mm});
            skLineSegment(sketch, "E0.0.318", {"start": v(-113.77, -110.17) * mm, "end": v(-114.32, -108.5) * mm});
            skLineSegment(sketch, "E0.0.319", {"start": v(-114.32, -108.5) * mm, "end": v(-114.57, -107.68) * mm});
            skLineSegment(sketch, "E0.0.320", {"start": v(-114.57, -107.68) * mm, "end": v(-114.7, -107.26) * mm});
            skLineSegment(sketch, "E0.0.321", {"start": v(-114.7, -107.26) * mm, "end": v(-114.81, -106.85) * mm});
            skLineSegment(sketch, "E0.0.322", {"start": v(-114.81, -106.85) * mm, "end": v(-119.37, -106.68) * mm});
            skLineSegment(sketch, "E0.0.323", {"start": v(-119.37, -106.68) * mm, "end": v(-119.52, -107.09) * mm});
            skLineSegment(sketch, "E0.0.324", {"start": v(-119.52, -107.09) * mm, "end": v(-119.67, -107.5) * mm});
            skLineSegment(sketch, "E0.0.325", {"start": v(-119.67, -107.5) * mm, "end": v(-119.98, -108.3) * mm});
            skLineSegment(sketch, "E0.0.326", {"start": v(-119.98, -108.3) * mm, "end": v(-120.64, -109.92) * mm});
            skLineSegment(sketch, "E0.0.327", {"start": v(-120.64, -109.92) * mm, "end": v(-121.36, -111.53) * mm});
            skLineSegment(sketch, "E0.0.328", {"start": v(-121.36, -111.53) * mm, "end": v(-122.11, -113.14) * mm});
            skLineSegment(sketch, "E0.0.329", {"start": v(-122.11, -113.14) * mm, "end": v(-126.5, -112.83) * mm});
            skLineSegment(sketch, "E0.0.330", {"start": v(-126.5, -112.83) * mm, "end": v(-127.03, -111.13) * mm});
            skLineSegment(sketch, "E0.0.331", {"start": v(-127.03, -111.13) * mm, "end": v(-127.5, -109.43) * mm});
            skLineSegment(sketch, "E0.0.332", {"start": v(-127.5, -109.43) * mm, "end": v(-127.93, -107.74) * mm});
            skLineSegment(sketch, "E0.0.333", {"start": v(-127.93, -107.74) * mm, "end": v(-128.13, -106.89) * mm});
            skLineSegment(sketch, "E0.0.334", {"start": v(-128.13, -106.89) * mm, "end": v(-128.22, -106.47) * mm});
            skLineSegment(sketch, "E0.0.335", {"start": v(-128.22, -106.47) * mm, "end": v(-128.3, -106.04) * mm});
            skLineSegment(sketch, "E0.0.336", {"start": v(-128.3, -106.04) * mm, "end": v(-132.84, -105.56) * mm});
            skLineSegment(sketch, "E0.0.337", {"start": v(-132.84, -105.56) * mm, "end": v(-133.02, -105.96) * mm});
            skLineSegment(sketch, "E0.0.338", {"start": v(-133.02, -105.96) * mm, "end": v(-133.2, -106.35) * mm});
            skLineSegment(sketch, "E0.0.339", {"start": v(-133.2, -106.35) * mm, "end": v(-133.57, -107.14) * mm});
            skLineSegment(sketch, "E0.0.340", {"start": v(-133.57, -107.14) * mm, "end": v(-134.34, -108.7) * mm});
            skLineSegment(sketch, "E0.0.341", {"start": v(-134.34, -108.7) * mm, "end": v(-135.16, -110.26) * mm});
            skLineSegment(sketch, "E0.0.342", {"start": v(-135.16, -110.26) * mm, "end": v(-136.03, -111.81) * mm});
            skLineSegment(sketch, "E0.0.343", {"start": v(-136.03, -111.81) * mm, "end": v(-140.4, -111.2) * mm});
            skLineSegment(sketch, "E0.0.344", {"start": v(-140.4, -111.2) * mm, "end": v(-140.8, -109.46) * mm});
            skLineSegment(sketch, "E0.0.345", {"start": v(-140.8, -109.46) * mm, "end": v(-141.15, -107.74) * mm});
            skLineSegment(sketch, "E0.0.346", {"start": v(-141.15, -107.74) * mm, "end": v(-141.46, -106.02) * mm});
            skLineSegment(sketch, "E0.0.347", {"start": v(-141.46, -106.02) * mm, "end": v(-141.6, -105.16) * mm});
            skLineSegment(sketch, "E0.0.348", {"start": v(-141.6, -105.16) * mm, "end": v(-141.66, -104.73) * mm});
            skLineSegment(sketch, "E0.0.349", {"start": v(-141.66, -104.73) * mm, "end": v(-141.72, -104.3) * mm});
            skLineSegment(sketch, "E0.0.350", {"start": v(-141.72, -104.3) * mm, "end": v(-146.2, -103.5) * mm});
            skLineSegment(sketch, "E0.0.351", {"start": v(-146.2, -103.5) * mm, "end": v(-146.4, -103.88) * mm});
            skLineSegment(sketch, "E0.0.352", {"start": v(-146.4, -103.88) * mm, "end": v(-146.61, -104.26) * mm});
            skLineSegment(sketch, "E0.0.353", {"start": v(-146.61, -104.26) * mm, "end": v(-147.04, -105.02) * mm});
            skLineSegment(sketch, "E0.0.354", {"start": v(-147.04, -105.02) * mm, "end": v(-147.92, -106.53) * mm});
            skLineSegment(sketch, "E0.0.355", {"start": v(-147.92, -106.53) * mm, "end": v(-148.85, -108.03) * mm});
            skLineSegment(sketch, "E0.0.356", {"start": v(-148.85, -108.03) * mm, "end": v(-149.82, -109.52) * mm});
            skLineSegment(sketch, "E0.0.357", {"start": v(-149.82, -109.52) * mm, "end": v(-154.13, -108.6) * mm});
            skLineSegment(sketch, "E0.0.358", {"start": v(-154.13, -108.6) * mm, "end": v(-154.4, -106.84) * mm});
            skLineSegment(sketch, "E0.0.359", {"start": v(-154.4, -106.84) * mm, "end": v(-154.64, -105.1) * mm});
            skLineSegment(sketch, "E0.0.360", {"start": v(-154.64, -105.1) * mm, "end": v(-154.83, -103.36) * mm});
            skLineSegment(sketch, "E0.0.361", {"start": v(-154.83, -103.36) * mm, "end": v(-154.9, -102.49) * mm});
            skLineSegment(sketch, "E0.0.362", {"start": v(-154.9, -102.49) * mm, "end": v(-154.94, -102.06) * mm});
            skLineSegment(sketch, "E0.0.363", {"start": v(-154.94, -102.06) * mm, "end": v(-154.97, -101.63) * mm});
            skLineSegment(sketch, "E0.0.364", {"start": v(-154.97, -101.63) * mm, "end": v(-159.4, -100.52) * mm});
            skLineSegment(sketch, "E0.0.365", {"start": v(-159.4, -100.52) * mm, "end": v(-159.62, -100.88) * mm});
            skLineSegment(sketch, "E0.0.366", {"start": v(-159.62, -100.88) * mm, "end": v(-159.85, -101.25) * mm});
            skLineSegment(sketch, "E0.0.367", {"start": v(-159.85, -101.25) * mm, "end": v(-160.33, -101.98) * mm});
            skLineSegment(sketch, "E0.0.368", {"start": v(-160.33, -101.98) * mm, "end": v(-161.31, -103.42) * mm});
            skLineSegment(sketch, "E0.0.369", {"start": v(-161.31, -103.42) * mm, "end": v(-162.34, -104.85) * mm});
            skLineSegment(sketch, "E0.0.370", {"start": v(-162.34, -104.85) * mm, "end": v(-163.42, -106.27) * mm});
            skLineSegment(sketch, "E0.0.371", {"start": v(-163.42, -106.27) * mm, "end": v(-167.65, -105.05) * mm});
            skLineSegment(sketch, "E0.0.372", {"start": v(-167.65, -105.05) * mm, "end": v(-167.8, -103.28) * mm});
            skLineSegment(sketch, "E0.0.373", {"start": v(-167.8, -103.28) * mm, "end": v(-167.92, -101.52) * mm});
            skLineSegment(sketch, "E0.0.374", {"start": v(-167.92, -101.52) * mm, "end": v(-167.99, -99.77) * mm});
            skLineSegment(sketch, "E0.0.375", {"start": v(-167.99, -99.77) * mm, "end": v(-168, -98.9) * mm});
            skLineSegment(sketch, "E0.0.376", {"start": v(-168, -98.9) * mm, "end": v(-168, -98.47) * mm});
            skLineSegment(sketch, "E0.0.377", {"start": v(-168, -98.47) * mm, "end": v(-168, -98.04) * mm});
            skLineSegment(sketch, "E0.0.378", {"start": v(-168, -98.04) * mm, "end": v(-172.34, -96.62) * mm});
            skLineSegment(sketch, "E0.0.379", {"start": v(-172.34, -96.62) * mm, "end": v(-172.6, -96.97) * mm});
            skLineSegment(sketch, "E0.0.380", {"start": v(-172.6, -96.97) * mm, "end": v(-172.85, -97.32) * mm});
            skLineSegment(sketch, "E0.0.381", {"start": v(-172.85, -97.32) * mm, "end": v(-173.37, -98.01) * mm});
            skLineSegment(sketch, "E0.0.382", {"start": v(-173.37, -98.01) * mm, "end": v(-174.46, -99.38) * mm});
            skLineSegment(sketch, "E0.0.383", {"start": v(-174.46, -99.38) * mm, "end": v(-175.59, -100.74) * mm});
            skLineSegment(sketch, "E0.0.384", {"start": v(-175.59, -100.74) * mm, "end": v(-176.76, -102.07) * mm});
            skLineSegment(sketch, "E0.0.385", {"start": v(-176.76, -102.07) * mm, "end": v(-180.9, -100.56) * mm});
            skLineSegment(sketch, "E0.0.386", {"start": v(-180.9, -100.56) * mm, "end": v(-180.93, -98.78) * mm});
            skLineSegment(sketch, "E0.0.387", {"start": v(-180.93, -98.78) * mm, "end": v(-180.92, -97.02) * mm});
            skLineSegment(sketch, "E0.0.388", {"start": v(-180.92, -97.02) * mm, "end": v(-180.86, -95.27) * mm});
            skLineSegment(sketch, "E0.0.389", {"start": v(-180.86, -95.27) * mm, "end": v(-180.81, -94.4) * mm});
            skLineSegment(sketch, "E0.0.390", {"start": v(-180.81, -94.4) * mm, "end": v(-180.79, -93.97) * mm});
            skLineSegment(sketch, "E0.0.391", {"start": v(-180.79, -93.97) * mm, "end": v(-180.75, -93.54) * mm});
            skLineSegment(sketch, "E0.0.392", {"start": v(-180.75, -93.54) * mm, "end": v(-184.98, -91.83) * mm});
            skLineSegment(sketch, "E0.0.393", {"start": v(-184.98, -91.83) * mm, "end": v(-185.26, -92.16) * mm});
            skLineSegment(sketch, "E0.0.394", {"start": v(-185.26, -92.16) * mm, "end": v(-185.54, -92.49) * mm});
            skLineSegment(sketch, "E0.0.395", {"start": v(-185.54, -92.49) * mm, "end": v(-186.11, -93.14) * mm});
            skLineSegment(sketch, "E0.0.396", {"start": v(-186.11, -93.14) * mm, "end": v(-187.29, -94.44) * mm});
            skLineSegment(sketch, "E0.0.397", {"start": v(-187.29, -94.44) * mm, "end": v(-188.5, -95.7) * mm});
            skLineSegment(sketch, "E0.0.398", {"start": v(-188.5, -95.7) * mm, "end": v(-189.77, -96.96) * mm});
            skLineSegment(sketch, "E0.0.399", {"start": v(-189.77, -96.96) * mm, "end": v(-193.79, -95.16) * mm});
            skLineSegment(sketch, "E0.0.400", {"start": v(-193.79, -95.16) * mm, "end": v(-193.7, -93.39) * mm});
            skLineSegment(sketch, "E0.0.401", {"start": v(-193.7, -93.39) * mm, "end": v(-193.57, -91.63) * mm});
            skLineSegment(sketch, "E0.0.402", {"start": v(-193.57, -91.63) * mm, "end": v(-193.39, -89.9) * mm});
            skLineSegment(sketch, "E0.0.403", {"start": v(-193.39, -89.9) * mm, "end": v(-193.28, -89.03) * mm});
            skLineSegment(sketch, "E0.0.404", {"start": v(-193.28, -89.03) * mm, "end": v(-193.22, -88.6) * mm});
            skLineSegment(sketch, "E0.0.405", {"start": v(-193.22, -88.6) * mm, "end": v(-193.16, -88.17) * mm});
            skLineSegment(sketch, "E0.0.406", {"start": v(-193.16, -88.17) * mm, "end": v(-197.26, -86.17) * mm});
            skLineSegment(sketch, "E0.0.407", {"start": v(-197.26, -86.17) * mm, "end": v(-197.56, -86.48) * mm});
            skLineSegment(sketch, "E0.0.408", {"start": v(-197.56, -86.48) * mm, "end": v(-197.86, -86.79) * mm});
            skLineSegment(sketch, "E0.0.409", {"start": v(-197.86, -86.79) * mm, "end": v(-198.48, -87.4) * mm});
            skLineSegment(sketch, "E0.0.410", {"start": v(-198.48, -87.4) * mm, "end": v(-199.74, -88.6) * mm});
            skLineSegment(sketch, "E0.0.411", {"start": v(-199.74, -88.6) * mm, "end": v(-201.05, -89.8) * mm});
            skLineSegment(sketch, "E0.0.412", {"start": v(-201.05, -89.8) * mm, "end": v(-202.4, -90.95) * mm});
            skLineSegment(sketch, "E0.0.413", {"start": v(-202.4, -90.95) * mm, "end": v(-206.28, -88.88) * mm});
            skLineSegment(sketch, "E0.0.414", {"start": v(-206.28, -88.88) * mm, "end": v(-206.06, -87.12) * mm});
            skLineSegment(sketch, "E0.0.415", {"start": v(-206.06, -87.12) * mm, "end": v(-205.8, -85.37) * mm});
            skLineSegment(sketch, "E0.0.416", {"start": v(-205.8, -85.37) * mm, "end": v(-205.5, -83.65) * mm});
            skLineSegment(sketch, "E0.0.417", {"start": v(-205.5, -83.65) * mm, "end": v(-205.34, -82.8) * mm});
            skLineSegment(sketch, "E0.0.418", {"start": v(-205.34, -82.8) * mm, "end": v(-205.26, -82.37) * mm});
            skLineSegment(sketch, "E0.0.419", {"start": v(-205.26, -82.37) * mm, "end": v(-205.17, -81.95) * mm});
            skLineSegment(sketch, "E0.0.420", {"start": v(-205.17, -81.95) * mm, "end": v(-209.11, -79.66) * mm});
            skLineSegment(sketch, "E0.0.421", {"start": v(-209.11, -79.66) * mm, "end": v(-209.43, -79.95) * mm});
            skLineSegment(sketch, "E0.0.422", {"start": v(-209.43, -79.95) * mm, "end": v(-209.76, -80.24) * mm});
            skLineSegment(sketch, "E0.0.423", {"start": v(-209.76, -80.24) * mm, "end": v(-210.41, -80.8) * mm});
            skLineSegment(sketch, "E0.0.424", {"start": v(-210.41, -80.8) * mm, "end": v(-211.76, -81.92) * mm});
            skLineSegment(sketch, "E0.0.425", {"start": v(-211.76, -81.92) * mm, "end": v(-213.14, -83.01) * mm});
            skLineSegment(sketch, "E0.0.426", {"start": v(-213.14, -83.01) * mm, "end": v(-214.57, -84.08) * mm});
            skLineSegment(sketch, "E0.0.427", {"start": v(-214.57, -84.08) * mm, "end": v(-218.3, -81.74) * mm});
            skLineSegment(sketch, "E0.0.428", {"start": v(-218.3, -81.74) * mm, "end": v(-217.96, -80) * mm});
            skLineSegment(sketch, "E0.0.429", {"start": v(-217.96, -80) * mm, "end": v(-217.58, -78.27) * mm});
            skLineSegment(sketch, "E0.0.430", {"start": v(-217.58, -78.27) * mm, "end": v(-217.17, -76.58) * mm});
            skLineSegment(sketch, "E0.0.431", {"start": v(-217.17, -76.58) * mm, "end": v(-216.94, -75.74) * mm});
            skLineSegment(sketch, "E0.0.432", {"start": v(-216.94, -75.74) * mm, "end": v(-216.82, -75.32) * mm});
            skLineSegment(sketch, "E0.0.433", {"start": v(-216.82, -75.32) * mm, "end": v(-216.7, -74.9) * mm});
            skLineSegment(sketch, "E0.0.434", {"start": v(-216.7, -74.9) * mm, "end": v(-220.48, -72.35) * mm});
            skLineSegment(sketch, "E0.0.435", {"start": v(-220.48, -72.35) * mm, "end": v(-220.82, -72.62) * mm});
            skLineSegment(sketch, "E0.0.436", {"start": v(-220.82, -72.62) * mm, "end": v(-221.16, -72.88) * mm});
            skLineSegment(sketch, "E0.0.437", {"start": v(-221.16, -72.88) * mm, "end": v(-221.86, -73.4) * mm});
            skLineSegment(sketch, "E0.0.438", {"start": v(-221.86, -73.4) * mm, "end": v(-223.28, -74.42) * mm});
            skLineSegment(sketch, "E0.0.439", {"start": v(-223.28, -74.42) * mm, "end": v(-224.74, -75.41) * mm});
            skLineSegment(sketch, "E0.0.440", {"start": v(-224.74, -75.41) * mm, "end": v(-226.23, -76.37) * mm});
            skLineSegment(sketch, "E0.0.441", {"start": v(-226.23, -76.37) * mm, "end": v(-229.8, -73.78) * mm});
            skLineSegment(sketch, "E0.0.442", {"start": v(-229.8, -73.78) * mm, "end": v(-229.33, -72.06) * mm});
            skLineSegment(sketch, "E0.0.443", {"start": v(-229.33, -72.06) * mm, "end": v(-228.84, -70.37) * mm});
            skLineSegment(sketch, "E0.0.444", {"start": v(-228.84, -70.37) * mm, "end": v(-228.3, -68.7) * mm});
            skLineSegment(sketch, "E0.0.445", {"start": v(-228.3, -68.7) * mm, "end": v(-228.02, -67.88) * mm});
            skLineSegment(sketch, "E0.0.446", {"start": v(-228.02, -67.88) * mm, "end": v(-227.87, -67.48) * mm});
            skLineSegment(sketch, "E0.0.447", {"start": v(-227.87, -67.48) * mm, "end": v(-227.72, -67.07) * mm});
            skLineSegment(sketch, "E0.0.448", {"start": v(-227.72, -67.07) * mm, "end": v(-231.31, -64.26) * mm});
            skLineSegment(sketch, "E0.0.449", {"start": v(-231.31, -64.26) * mm, "end": v(-231.67, -64.5) * mm});
            skLineSegment(sketch, "E0.0.450", {"start": v(-231.67, -64.5) * mm, "end": v(-232.03, -64.74) * mm});
            skLineSegment(sketch, "E0.0.451", {"start": v(-232.03, -64.74) * mm, "end": v(-232.76, -65.21) * mm});
            skLineSegment(sketch, "E0.0.452", {"start": v(-232.76, -65.21) * mm, "end": v(-234.25, -66.13) * mm});
            skLineSegment(sketch, "E0.0.453", {"start": v(-234.25, -66.13) * mm, "end": v(-235.77, -67.02) * mm});
            skLineSegment(sketch, "E0.0.454", {"start": v(-235.77, -67.02) * mm, "end": v(-237.33, -67.87) * mm});
            skLineSegment(sketch, "E0.0.455", {"start": v(-237.33, -67.87) * mm, "end": v(-240.7, -65.04) * mm});
            skLineSegment(sketch, "E0.0.456", {"start": v(-240.7, -65.04) * mm, "end": v(-240.12, -63.35) * mm});
            skLineSegment(sketch, "E0.0.457", {"start": v(-240.12, -63.35) * mm, "end": v(-239.51, -61.7) * mm});
            skLineSegment(sketch, "E0.0.458", {"start": v(-239.51, -61.7) * mm, "end": v(-238.86, -60.08) * mm});
            skLineSegment(sketch, "E0.0.459", {"start": v(-238.86, -60.08) * mm, "end": v(-238.52, -59.28) * mm});
            skLineSegment(sketch, "E0.0.460", {"start": v(-238.52, -59.28) * mm, "end": v(-238.35, -58.88) * mm});
            skLineSegment(sketch, "E0.0.461", {"start": v(-238.35, -58.88) * mm, "end": v(-238.17, -58.49) * mm});
            skLineSegment(sketch, "E0.0.462", {"start": v(-238.17, -58.49) * mm, "end": v(-241.55, -55.43) * mm});
            skLineSegment(sketch, "E0.0.463", {"start": v(-241.55, -55.43) * mm, "end": v(-241.93, -55.65) * mm});
            skLineSegment(sketch, "E0.0.464", {"start": v(-241.93, -55.65) * mm, "end": v(-242.3, -55.86) * mm});
            skLineSegment(sketch, "E0.0.465", {"start": v(-242.3, -55.86) * mm, "end": v(-243.07, -56.28) * mm});
            skLineSegment(sketch, "E0.0.466", {"start": v(-243.07, -56.28) * mm, "end": v(-244.61, -57.1) * mm});
            skLineSegment(sketch, "E0.0.467", {"start": v(-244.61, -57.1) * mm, "end": v(-246.2, -57.87) * mm});
            skLineSegment(sketch, "E0.0.468", {"start": v(-246.2, -57.87) * mm, "end": v(-247.81, -58.62) * mm});
            skLineSegment(sketch, "E0.0.469", {"start": v(-247.81, -58.62) * mm, "end": v(-250.97, -55.55) * mm});
            skLineSegment(sketch, "E0.0.470", {"start": v(-250.97, -55.55) * mm, "end": v(-250.28, -53.92) * mm});
            skLineSegment(sketch, "E0.0.471", {"start": v(-250.28, -53.92) * mm, "end": v(-249.55, -52.3) * mm});
            skLineSegment(sketch, "E0.0.472", {"start": v(-249.55, -52.3) * mm, "end": v(-248.8, -50.74) * mm});
            skLineSegment(sketch, "E0.0.473", {"start": v(-248.8, -50.74) * mm, "end": v(-248.4, -49.96) * mm});
            skLineSegment(sketch, "E0.0.474", {"start": v(-248.4, -49.96) * mm, "end": v(-248.2, -49.58) * mm});
            skLineSegment(sketch, "E0.0.475", {"start": v(-248.2, -49.58) * mm, "end": v(-248, -49.2) * mm});
            skLineSegment(sketch, "E0.0.476", {"start": v(-248, -49.2) * mm, "end": v(-251.16, -45.91) * mm});
            skLineSegment(sketch, "E0.0.477", {"start": v(-251.16, -45.91) * mm, "end": v(-251.54, -46.1) * mm});
            skLineSegment(sketch, "E0.0.478", {"start": v(-251.54, -46.1) * mm, "end": v(-251.94, -46.29) * mm});
            skLineSegment(sketch, "E0.0.479", {"start": v(-251.94, -46.29) * mm, "end": v(-252.72, -46.65) * mm});
            skLineSegment(sketch, "E0.0.480", {"start": v(-252.72, -46.65) * mm, "end": v(-254.32, -47.36) * mm});
            skLineSegment(sketch, "E0.0.481", {"start": v(-254.32, -47.36) * mm, "end": v(-255.96, -48.02) * mm});
            skLineSegment(sketch, "E0.0.482", {"start": v(-255.96, -48.02) * mm, "end": v(-257.62, -48.65) * mm});
            skLineSegment(sketch, "E0.0.483", {"start": v(-257.62, -48.65) * mm, "end": v(-260.56, -45.38) * mm});
            skLineSegment(sketch, "E0.0.484", {"start": v(-260.56, -45.38) * mm, "end": v(-259.76, -43.8) * mm});
            skLineSegment(sketch, "E0.0.485", {"start": v(-259.76, -43.8) * mm, "end": v(-258.92, -42.24) * mm});
            skLineSegment(sketch, "E0.0.486", {"start": v(-258.92, -42.24) * mm, "end": v(-258.05, -40.72) * mm});
            skLineSegment(sketch, "E0.0.487", {"start": v(-258.05, -40.72) * mm, "end": v(-257.6, -39.98) * mm});
            skLineSegment(sketch, "E0.0.488", {"start": v(-257.6, -39.98) * mm, "end": v(-257.37, -39.61) * mm});
            skLineSegment(sketch, "E0.0.489", {"start": v(-257.37, -39.61) * mm, "end": v(-257.14, -39.25) * mm});
            skLineSegment(sketch, "E0.0.490", {"start": v(-257.14, -39.25) * mm, "end": v(-260.07, -35.75) * mm});
            skLineSegment(sketch, "E0.0.491", {"start": v(-260.07, -35.75) * mm, "end": v(-260.47, -35.9) * mm});
            skLineSegment(sketch, "E0.0.492", {"start": v(-260.47, -35.9) * mm, "end": v(-260.87, -36.07) * mm});
            skLineSegment(sketch, "E0.0.493", {"start": v(-260.87, -36.07) * mm, "end": v(-261.68, -36.38) * mm});
            skLineSegment(sketch, "E0.0.494", {"start": v(-261.68, -36.38) * mm, "end": v(-263.33, -36.97) * mm});
            skLineSegment(sketch, "E0.0.495", {"start": v(-263.33, -36.97) * mm, "end": v(-265, -37.52) * mm});
            skLineSegment(sketch, "E0.0.496", {"start": v(-265, -37.52) * mm, "end": v(-266.7, -38.03) * mm});
            skLineSegment(sketch, "E0.0.497", {"start": v(-266.7, -38.03) * mm, "end": v(-269.41, -34.56) * mm});
            skLineSegment(sketch, "E0.0.498", {"start": v(-269.41, -34.56) * mm, "end": v(-268.5, -33.03) * mm});
            skLineSegment(sketch, "E0.0.499", {"start": v(-268.5, -33.03) * mm, "end": v(-267.56, -31.54) * mm});
            skLineSegment(sketch, "E0.0.500", {"start": v(-267.56, -31.54) * mm, "end": v(-266.58, -30.1) * mm});
            skLineSegment(sketch, "E0.0.501", {"start": v(-266.58, -30.1) * mm, "end": v(-266.08, -29.38) * mm});
            skLineSegment(sketch, "E0.0.502", {"start": v(-266.08, -29.38) * mm, "end": v(-265.83, -29.03) * mm});
            skLineSegment(sketch, "E0.0.503", {"start": v(-265.83, -29.03) * mm, "end": v(-265.58, -28.68) * mm});
            skLineSegment(sketch, "E0.0.504", {"start": v(-265.58, -28.68) * mm, "end": v(-268.25, -24.99) * mm});
            skLineSegment(sketch, "E0.0.505", {"start": v(-268.25, -24.99) * mm, "end": v(-268.66, -25.12) * mm});
            skLineSegment(sketch, "E0.0.506", {"start": v(-268.66, -25.12) * mm, "end": v(-269.08, -25.25) * mm});
            skLineSegment(sketch, "E0.0.507", {"start": v(-269.08, -25.25) * mm, "end": v(-269.9, -25.5) * mm});
            skLineSegment(sketch, "E0.0.508", {"start": v(-269.9, -25.5) * mm, "end": v(-271.6, -25.97) * mm});
            skLineSegment(sketch, "E0.0.509", {"start": v(-271.6, -25.97) * mm, "end": v(-273.3, -26.4) * mm});
            skLineSegment(sketch, "E0.0.510", {"start": v(-273.3, -26.4) * mm, "end": v(-275.03, -26.8) * mm});
            skLineSegment(sketch, "E0.0.511", {"start": v(-275.03, -26.8) * mm, "end": v(-277.5, -23.14) * mm});
            skLineSegment(sketch, "E0.0.512", {"start": v(-277.5, -23.14) * mm, "end": v(-276.47, -21.69) * mm});
            skLineSegment(sketch, "E0.0.513", {"start": v(-276.47, -21.69) * mm, "end": v(-275.43, -20.27) * mm});
            skLineSegment(sketch, "E0.0.514", {"start": v(-275.43, -20.27) * mm, "end": v(-274.36, -18.89) * mm});
            skLineSegment(sketch, "E0.0.515", {"start": v(-274.36, -18.89) * mm, "end": v(-273.8, -18.21) * mm});
            skLineSegment(sketch, "E0.0.516", {"start": v(-273.8, -18.21) * mm, "end": v(-273.53, -17.88) * mm});
            skLineSegment(sketch, "E0.0.517", {"start": v(-273.53, -17.88) * mm, "end": v(-273.25, -17.55) * mm});
            skLineSegment(sketch, "E0.0.518", {"start": v(-273.25, -17.55) * mm, "end": v(-275.66, -13.68) * mm});
            skLineSegment(sketch, "E0.0.519", {"start": v(-275.66, -13.68) * mm, "end": v(-276.08, -13.78) * mm});
            skLineSegment(sketch, "E0.0.520", {"start": v(-276.08, -13.78) * mm, "end": v(-276.5, -13.88) * mm});
            skLineSegment(sketch, "E0.0.521", {"start": v(-276.5, -13.88) * mm, "end": v(-277.35, -14.08) * mm});
            skLineSegment(sketch, "E0.0.522", {"start": v(-277.35, -14.08) * mm, "end": v(-279.06, -14.43) * mm});
            skLineSegment(sketch, "E0.0.523", {"start": v(-279.06, -14.43) * mm, "end": v(-280.8, -14.74) * mm});
            skLineSegment(sketch, "E0.0.524", {"start": v(-280.8, -14.74) * mm, "end": v(-282.56, -15.01) * mm});
            skLineSegment(sketch, "E0.0.525", {"start": v(-282.56, -15.01) * mm, "end": v(-284.75, -11.2) * mm});
            skLineSegment(sketch, "E0.0.526", {"start": v(-284.75, -11.2) * mm, "end": v(-283.63, -9.81) * mm});
            skLineSegment(sketch, "E0.0.527", {"start": v(-283.63, -9.81) * mm, "end": v(-282.5, -8.47) * mm});
            skLineSegment(sketch, "E0.0.528", {"start": v(-282.5, -8.47) * mm, "end": v(-281.33, -7.17) * mm});
            skLineSegment(sketch, "E0.0.529", {"start": v(-281.33, -7.17) * mm, "end": v(-280.73, -6.53) * mm});
            skLineSegment(sketch, "E0.0.530", {"start": v(-280.73, -6.53) * mm, "end": v(-280.44, -6.22) * mm});
            skLineSegment(sketch, "E0.0.531", {"start": v(-280.44, -6.22) * mm, "end": v(-280.14, -5.91) * mm});
            skLineSegment(sketch, "E0.0.532", {"start": v(-280.14, -5.91) * mm, "end": v(-282.27, -1.88) * mm});
            skLineSegment(sketch, "E0.0.533", {"start": v(-282.27, -1.88) * mm, "end": v(-282.7, -1.96) * mm});
            skLineSegment(sketch, "E0.0.534", {"start": v(-282.7, -1.96) * mm, "end": v(-283.12, -2.03) * mm});
            skLineSegment(sketch, "E0.0.535", {"start": v(-283.12, -2.03) * mm, "end": v(-283.98, -2.16) * mm});
            skLineSegment(sketch, "E0.0.536", {"start": v(-283.98, -2.16) * mm, "end": v(-285.71, -2.4) * mm});
            skLineSegment(sketch, "E0.0.537", {"start": v(-285.71, -2.4) * mm, "end": v(-287.47, -2.59) * mm});
            skLineSegment(sketch, "E0.0.538", {"start": v(-287.47, -2.59) * mm, "end": v(-289.24, -2.73) * mm});
            skLineSegment(sketch, "E0.0.539", {"start": v(-289.24, -2.73) * mm, "end": v(-291.16, 1.23) * mm});
            skLineSegment(sketch, "E0.0.540", {"start": v(-291.16, 1.23) * mm, "end": v(-289.95, 2.53) * mm});
            skLineSegment(sketch, "E0.0.541", {"start": v(-289.95, 2.53) * mm, "end": v(-288.72, 3.79) * mm});
            skLineSegment(sketch, "E0.0.542", {"start": v(-288.72, 3.79) * mm, "end": v(-287.46, 5) * mm});
            skLineSegment(sketch, "E0.0.543", {"start": v(-287.46, 5) * mm, "end": v(-286.83, 5.6) * mm});
            skLineSegment(sketch, "E0.0.544", {"start": v(-286.83, 5.6) * mm, "end": v(-286.5, 5.9) * mm});
            skLineSegment(sketch, "E0.0.545", {"start": v(-286.5, 5.9) * mm, "end": v(-286.19, 6.18) * mm});
            skLineSegment(sketch, "E0.0.546", {"start": v(-286.19, 6.18) * mm, "end": v(-288.04, 10.35) * mm});
            skLineSegment(sketch, "E0.0.547", {"start": v(-288.04, 10.35) * mm, "end": v(-288.47, 10.3) * mm});
            skLineSegment(sketch, "E0.0.548", {"start": v(-288.47, 10.3) * mm, "end": v(-288.9, 10.26) * mm});
            skLineSegment(sketch, "E0.0.549", {"start": v(-288.9, 10.26) * mm, "end": v(-289.76, 10.19) * mm});
            skLineSegment(sketch, "E0.0.550", {"start": v(-289.76, 10.19) * mm, "end": v(-291.5, 10.07) * mm});
            skLineSegment(sketch, "E0.0.551", {"start": v(-291.5, 10.07) * mm, "end": v(-293.27, 10) * mm});
            skLineSegment(sketch, "E0.0.552", {"start": v(-293.27, 10) * mm, "end": v(-295.05, 9.98) * mm});
            skLineSegment(sketch, "E0.0.553", {"start": v(-295.05, 9.98) * mm, "end": v(-296.69, 14.07) * mm});
            skLineSegment(sketch, "E0.0.554", {"start": v(-296.69, 14.07) * mm, "end": v(-295.4, 15.28) * mm});
            skLineSegment(sketch, "E0.0.555", {"start": v(-295.4, 15.28) * mm, "end": v(-294.07, 16.45) * mm});
            skLineSegment(sketch, "E0.0.556", {"start": v(-294.07, 16.45) * mm, "end": v(-292.74, 17.58) * mm});
            skLineSegment(sketch, "E0.0.557", {"start": v(-292.74, 17.58) * mm, "end": v(-292.06, 18.13) * mm});
            skLineSegment(sketch, "E0.0.558", {"start": v(-292.06, 18.13) * mm, "end": v(-291.72, 18.4) * mm});
            skLineSegment(sketch, "E0.0.559", {"start": v(-291.72, 18.4) * mm, "end": v(-291.38, 18.66) * mm});
            skLineSegment(sketch, "E0.0.560", {"start": v(-291.38, 18.66) * mm, "end": v(-292.94, 22.95) * mm});
            skLineSegment(sketch, "E0.0.561", {"start": v(-292.94, 22.95) * mm, "end": v(-293.37, 22.93) * mm});
            skLineSegment(sketch, "E0.0.562", {"start": v(-293.37, 22.93) * mm, "end": v(-293.8, 22.92) * mm});
            skLineSegment(sketch, "E0.0.563", {"start": v(-293.8, 22.92) * mm, "end": v(-294.67, 22.9) * mm});
            skLineSegment(sketch, "E0.0.564", {"start": v(-294.67, 22.9) * mm, "end": v(-296.42, 22.92) * mm});
            skLineSegment(sketch, "E0.0.565", {"start": v(-296.42, 22.92) * mm, "end": v(-298.18, 22.97) * mm});
            skLineSegment(sketch, "E0.0.566", {"start": v(-298.18, 22.97) * mm, "end": v(-299.95, 23.07) * mm});
            skLineSegment(sketch, "E0.0.567", {"start": v(-299.95, 23.07) * mm, "end": v(-301.3, 27.26) * mm});
            skLineSegment(sketch, "E0.0.568", {"start": v(-301.3, 27.26) * mm, "end": v(-299.93, 28.38) * mm});
            skLineSegment(sketch, "E0.0.569", {"start": v(-299.93, 28.38) * mm, "end": v(-298.53, 29.46) * mm});
            skLineSegment(sketch, "E0.0.570", {"start": v(-298.53, 29.46) * mm, "end": v(-297.12, 30.5) * mm});
            skLineSegment(sketch, "E0.0.571", {"start": v(-297.12, 30.5) * mm, "end": v(-296.4, 31) * mm});
            skLineSegment(sketch, "E0.0.572", {"start": v(-296.4, 31) * mm, "end": v(-296.05, 31.24) * mm});
            skLineSegment(sketch, "E0.0.573", {"start": v(-296.05, 31.24) * mm, "end": v(-295.7, 31.48) * mm});
            skLineSegment(sketch, "E0.0.574", {"start": v(-295.7, 31.48) * mm, "end": v(-296.94, 35.86) * mm});
            skLineSegment(sketch, "E0.0.575", {"start": v(-296.94, 35.86) * mm, "end": v(-297.38, 35.88) * mm});
            skLineSegment(sketch, "E0.0.576", {"start": v(-297.38, 35.88) * mm, "end": v(-297.8, 35.9) * mm});
            skLineSegment(sketch, "E0.0.577", {"start": v(-297.8, 35.9) * mm, "end": v(-298.68, 35.94) * mm});
            skLineSegment(sketch, "E0.0.578", {"start": v(-298.68, 35.94) * mm, "end": v(-300.42, 36.07) * mm});
            skLineSegment(sketch, "E0.0.579", {"start": v(-300.42, 36.07) * mm, "end": v(-302.17, 36.25) * mm});
            skLineSegment(sketch, "E0.0.580", {"start": v(-302.17, 36.25) * mm, "end": v(-303.94, 36.48) * mm});
            skLineSegment(sketch, "E0.0.581", {"start": v(-303.94, 36.48) * mm, "end": v(-305, 40.75) * mm});
            skLineSegment(sketch, "E0.0.582", {"start": v(-305, 40.75) * mm, "end": v(-303.54, 41.77) * mm});
            skLineSegment(sketch, "E0.0.583", {"start": v(-303.54, 41.77) * mm, "end": v(-302.07, 42.75) * mm});
            skLineSegment(sketch, "E0.0.584", {"start": v(-302.07, 42.75) * mm, "end": v(-300.6, 43.68) * mm});
            skLineSegment(sketch, "E0.0.585", {"start": v(-300.6, 43.68) * mm, "end": v(-299.85, 44.13) * mm});
            skLineSegment(sketch, "E0.0.586", {"start": v(-299.85, 44.13) * mm, "end": v(-299.47, 44.34) * mm});
            skLineSegment(sketch, "E0.0.587", {"start": v(-299.47, 44.34) * mm, "end": v(-299.1, 44.56) * mm});
            skLineSegment(sketch, "E0.0.588", {"start": v(-299.1, 44.56) * mm, "end": v(-300.04, 49.02) * mm});
            skLineSegment(sketch, "E0.0.589", {"start": v(-300.04, 49.02) * mm, "end": v(-300.47, 49.07) * mm});
            skLineSegment(sketch, "E0.0.590", {"start": v(-300.47, 49.07) * mm, "end": v(-300.9, 49.12) * mm});
            skLineSegment(sketch, "E0.0.591", {"start": v(-300.9, 49.12) * mm, "end": v(-301.76, 49.22) * mm});
            skLineSegment(sketch, "E0.0.592", {"start": v(-301.76, 49.22) * mm, "end": v(-303.5, 49.48) * mm});
            skLineSegment(sketch, "E0.0.593", {"start": v(-303.5, 49.48) * mm, "end": v(-305.23, 49.78) * mm});
            skLineSegment(sketch, "E0.0.594", {"start": v(-305.23, 49.78) * mm, "end": v(-306.97, 50.12) * mm});
            skLineSegment(sketch, "E0.0.595", {"start": v(-306.97, 50.12) * mm, "end": v(-307.73, 54.46) * mm});
            skLineSegment(sketch, "E0.0.596", {"start": v(-307.73, 54.46) * mm, "end": v(-306.2, 55.38) * mm});
            skLineSegment(sketch, "E0.0.597", {"start": v(-306.2, 55.38) * mm, "end": v(-304.68, 56.25) * mm});
            skLineSegment(sketch, "E0.0.598", {"start": v(-304.68, 56.25) * mm, "end": v(-303.14, 57.07) * mm});
            skLineSegment(sketch, "E0.0.599", {"start": v(-303.14, 57.07) * mm, "end": v(-302.36, 57.47) * mm});
            skLineSegment(sketch, "E0.0.600", {"start": v(-302.36, 57.47) * mm, "end": v(-301.97, 57.66) * mm});
            skLineSegment(sketch, "E0.0.601", {"start": v(-301.97, 57.66) * mm, "end": v(-301.59, 57.85) * mm});
            skLineSegment(sketch, "E0.0.602", {"start": v(-301.59, 57.85) * mm, "end": v(-302.21, 62.37) * mm});
            skLineSegment(sketch, "E0.0.603", {"start": v(-302.21, 62.37) * mm, "end": v(-302.64, 62.44) * mm});
            skLineSegment(sketch, "E0.0.604", {"start": v(-302.64, 62.44) * mm, "end": v(-303.06, 62.52) * mm});
            skLineSegment(sketch, "E0.0.605", {"start": v(-303.06, 62.52) * mm, "end": v(-303.92, 62.69) * mm});
            skLineSegment(sketch, "E0.0.606", {"start": v(-303.92, 62.69) * mm, "end": v(-305.62, 63.06) * mm});
            skLineSegment(sketch, "E0.0.607", {"start": v(-305.62, 63.06) * mm, "end": v(-307.34, 63.48) * mm});
            skLineSegment(sketch, "E0.0.608", {"start": v(-307.34, 63.48) * mm, "end": v(-309.05, 63.95) * mm});
            skLineSegment(sketch, "E0.0.609", {"start": v(-309.05, 63.95) * mm, "end": v(-309.5, 68.33) * mm});
            skLineSegment(sketch, "E0.0.610", {"start": v(-309.5, 68.33) * mm, "end": v(-307.92, 69.14) * mm});
            skLineSegment(sketch, "E0.0.611", {"start": v(-307.92, 69.14) * mm, "end": v(-306.33, 69.9) * mm});
            skLineSegment(sketch, "E0.0.612", {"start": v(-306.33, 69.9) * mm, "end": v(-304.74, 70.62) * mm});
            skLineSegment(sketch, "E0.0.613", {"start": v(-304.74, 70.62) * mm, "end": v(-303.94, 70.95) * mm});
            skLineSegment(sketch, "E0.0.614", {"start": v(-303.94, 70.95) * mm, "end": v(-303.54, 71.12) * mm});
            skLineSegment(sketch, "E0.0.615", {"start": v(-303.54, 71.12) * mm, "end": v(-303.14, 71.28) * mm});
            skLineSegment(sketch, "E0.0.616", {"start": v(-303.14, 71.28) * mm, "end": v(-303.45, 75.83) * mm});
            skLineSegment(sketch, "E0.0.617", {"start": v(-303.45, 75.83) * mm, "end": v(-303.87, 75.93) * mm});
            skLineSegment(sketch, "E0.0.618", {"start": v(-303.87, 75.93) * mm, "end": v(-304.29, 76.04) * mm});
            skLineSegment(sketch, "E0.0.619", {"start": v(-304.29, 76.04) * mm, "end": v(-305.13, 76.27) * mm});
            skLineSegment(sketch, "E0.0.620", {"start": v(-305.13, 76.27) * mm, "end": v(-306.8, 76.76) * mm});
            skLineSegment(sketch, "E0.0.621", {"start": v(-306.8, 76.76) * mm, "end": v(-308.48, 77.3) * mm});
            skLineSegment(sketch, "E0.0.622", {"start": v(-308.48, 77.3) * mm, "end": v(-310.16, 77.88) * mm});
            skLineSegment(sketch, "E0.0.623", {"start": v(-310.16, 77.88) * mm, "end": v(-310.3, 82.29) * mm});
            skLineSegment(sketch, "E0.0.624", {"start": v(-310.3, 82.29) * mm, "end": v(-308.67, 82.98) * mm});
            skLineSegment(sketch, "E0.0.625", {"start": v(-308.67, 82.98) * mm, "end": v(-307.03, 83.63) * mm});
            skLineSegment(sketch, "E0.0.626", {"start": v(-307.03, 83.63) * mm, "end": v(-305.4, 84.23) * mm});
            skLineSegment(sketch, "E0.0.627", {"start": v(-305.4, 84.23) * mm, "end": v(-304.57, 84.52) * mm});
            skLineSegment(sketch, "E0.0.628", {"start": v(-304.57, 84.52) * mm, "end": v(-304.16, 84.65) * mm});
            skLineSegment(sketch, "E0.0.629", {"start": v(-304.16, 84.65) * mm, "end": v(-303.75, 84.79) * mm});
            skLineSegment(sketch, "E0.0.630", {"start": v(-303.75, 84.79) * mm, "end": v(-303.74, 89.35) * mm});
            skLineSegment(sketch, "E0.0.631", {"start": v(-303.74, 89.35) * mm, "end": v(-304.15, 89.48) * mm});
            skLineSegment(sketch, "E0.0.632", {"start": v(-304.15, 89.48) * mm, "end": v(-304.57, 89.62) * mm});
            skLineSegment(sketch, "E0.0.633", {"start": v(-304.57, 89.62) * mm, "end": v(-305.39, 89.9) * mm});
            skLineSegment(sketch, "E0.0.634", {"start": v(-305.39, 89.9) * mm, "end": v(-307.03, 90.5) * mm});
            skLineSegment(sketch, "E0.0.635", {"start": v(-307.03, 90.5) * mm, "end": v(-308.66, 91.16) * mm});
            skLineSegment(sketch, "E0.0.636", {"start": v(-308.66, 91.16) * mm, "end": v(-310.3, 91.86) * mm});
            skLineSegment(sketch, "E0.0.637", {"start": v(-310.3, 91.86) * mm, "end": v(-310.14, 96.27) * mm});
            skLineSegment(sketch, "E0.0.638", {"start": v(-310.14, 96.27) * mm, "end": v(-308.46, 96.85) * mm});
            skLineSegment(sketch, "E0.0.639", {"start": v(-308.46, 96.85) * mm, "end": v(-306.78, 97.38) * mm});
            skLineSegment(sketch, "E0.0.640", {"start": v(-306.78, 97.38) * mm, "end": v(-305.1, 97.87) * mm});
            skLineSegment(sketch, "E0.0.641", {"start": v(-305.1, 97.87) * mm, "end": v(-304.26, 98.1) * mm});
            skLineSegment(sketch, "E0.0.642", {"start": v(-304.26, 98.1) * mm, "end": v(-303.84, 98.2) * mm});
            skLineSegment(sketch, "E0.0.643", {"start": v(-303.84, 98.2) * mm, "end": v(-303.42, 98.3) * mm});
            skLineSegment(sketch, "E0.0.644", {"start": v(-303.42, 98.3) * mm, "end": v(-303.1, 102.85) * mm});
            skLineSegment(sketch, "E0.0.645", {"start": v(-303.1, 102.85) * mm, "end": v(-303.5, 103.01) * mm});
            skLineSegment(sketch, "E0.0.646", {"start": v(-303.5, 103.01) * mm, "end": v(-303.9, 103.18) * mm});
            skLineSegment(sketch, "E0.0.647", {"start": v(-303.9, 103.18) * mm, "end": v(-304.7, 103.52) * mm});
            skLineSegment(sketch, "E0.0.648", {"start": v(-304.7, 103.52) * mm, "end": v(-306.29, 104.24) * mm});
            skLineSegment(sketch, "E0.0.649", {"start": v(-306.29, 104.24) * mm, "end": v(-307.87, 105) * mm});
            skLineSegment(sketch, "E0.0.650", {"start": v(-307.87, 105) * mm, "end": v(-309.45, 105.82) * mm});
            skLineSegment(sketch, "E0.0.651", {"start": v(-309.45, 105.82) * mm, "end": v(-308.99, 110.2) * mm});
            skLineSegment(sketch, "E0.0.652", {"start": v(-308.99, 110.2) * mm, "end": v(-307.27, 110.66) * mm});
            skLineSegment(sketch, "E0.0.653", {"start": v(-307.27, 110.66) * mm, "end": v(-305.56, 111.08) * mm});
            skLineSegment(sketch, "E0.0.654", {"start": v(-305.56, 111.08) * mm, "end": v(-303.85, 111.44) * mm});
            skLineSegment(sketch, "E0.0.655", {"start": v(-303.85, 111.44) * mm, "end": v(-303, 111.61) * mm});
            skLineSegment(sketch, "E0.0.656", {"start": v(-303, 111.61) * mm, "end": v(-302.57, 111.69) * mm});
            skLineSegment(sketch, "E0.0.657", {"start": v(-302.57, 111.69) * mm, "end": v(-302.14, 111.76) * mm});
            skLineSegment(sketch, "E0.0.658", {"start": v(-302.14, 111.76) * mm, "end": v(-301.5, 116.28) * mm});
            skLineSegment(sketch, "E0.0.659", {"start": v(-301.5, 116.28) * mm, "end": v(-301.9, 116.47) * mm});
            skLineSegment(sketch, "E0.0.660", {"start": v(-301.9, 116.47) * mm, "end": v(-302.28, 116.66) * mm});
            skLineSegment(sketch, "E0.0.661", {"start": v(-302.28, 116.66) * mm, "end": v(-303.05, 117.06) * mm});
            skLineSegment(sketch, "E0.0.662", {"start": v(-303.05, 117.06) * mm, "end": v(-304.6, 117.88) * mm});
            skLineSegment(sketch, "E0.0.663", {"start": v(-304.6, 117.88) * mm, "end": v(-306.12, 118.76) * mm});
            skLineSegment(sketch, "E0.0.664", {"start": v(-306.12, 118.76) * mm, "end": v(-307.64, 119.68) * mm});
            skLineSegment(sketch, "E0.0.665", {"start": v(-307.64, 119.68) * mm, "end": v(-306.87, 124.02) * mm});
            skLineSegment(sketch, "E0.0.666", {"start": v(-306.87, 124.02) * mm, "end": v(-305.13, 124.36) * mm});
            skLineSegment(sketch, "E0.0.667", {"start": v(-305.13, 124.36) * mm, "end": v(-303.39, 124.65) * mm});
            skLineSegment(sketch, "E0.0.668", {"start": v(-303.39, 124.65) * mm, "end": v(-301.66, 124.9) * mm});
            skLineSegment(sketch, "E0.0.669", {"start": v(-301.66, 124.9) * mm, "end": v(-300.8, 125) * mm});
            skLineSegment(sketch, "E0.0.670", {"start": v(-300.8, 125) * mm, "end": v(-300.37, 125.06) * mm});
            skLineSegment(sketch, "E0.0.671", {"start": v(-300.37, 125.06) * mm, "end": v(-299.94, 125.1) * mm});
            skLineSegment(sketch, "E0.0.672", {"start": v(-299.94, 125.1) * mm, "end": v(-298.98, 129.56) * mm});
            skLineSegment(sketch, "E0.0.673", {"start": v(-298.98, 129.56) * mm, "end": v(-299.36, 129.78) * mm});
            skLineSegment(sketch, "E0.0.674", {"start": v(-299.36, 129.78) * mm, "end": v(-299.73, 130) * mm});
            skLineSegment(sketch, "E0.0.675", {"start": v(-299.73, 130) * mm, "end": v(-300.47, 130.44) * mm});
            skLineSegment(sketch, "E0.0.676", {"start": v(-300.47, 130.44) * mm, "end": v(-301.95, 131.38) * mm});
            skLineSegment(sketch, "E0.0.677", {"start": v(-301.95, 131.38) * mm, "end": v(-303.41, 132.36) * mm});
            skLineSegment(sketch, "E0.0.678", {"start": v(-303.41, 132.36) * mm, "end": v(-304.87, 133.39) * mm});
            skLineSegment(sketch, "E0.0.679", {"start": v(-304.87, 133.39) * mm, "end": v(-303.8, 137.66) * mm});
            skLineSegment(sketch, "E0.0.680", {"start": v(-303.8, 137.66) * mm, "end": v(-302.03, 137.87) * mm});
            skLineSegment(sketch, "E0.0.681", {"start": v(-302.03, 137.87) * mm, "end": v(-300.28, 138.05) * mm});
            skLineSegment(sketch, "E0.0.682", {"start": v(-300.28, 138.05) * mm, "end": v(-298.53, 138.18) * mm});
            skLineSegment(sketch, "E0.0.683", {"start": v(-298.53, 138.18) * mm, "end": v(-297.67, 138.22) * mm});
            skLineSegment(sketch, "E0.0.684", {"start": v(-297.67, 138.22) * mm, "end": v(-297.23, 138.24) * mm});
            skLineSegment(sketch, "E0.0.685", {"start": v(-297.23, 138.24) * mm, "end": v(-296.8, 138.25) * mm});
            skLineSegment(sketch, "E0.0.686", {"start": v(-296.8, 138.25) * mm, "end": v(-295.54, 142.63) * mm});
            skLineSegment(sketch, "E0.0.687", {"start": v(-295.54, 142.63) * mm, "end": v(-295.9, 142.88) * mm});
            skLineSegment(sketch, "E0.0.688", {"start": v(-295.9, 142.88) * mm, "end": v(-296.25, 143.12) * mm});
            skLineSegment(sketch, "E0.0.689", {"start": v(-296.25, 143.12) * mm, "end": v(-296.96, 143.62) * mm});
            skLineSegment(sketch, "E0.0.690", {"start": v(-296.96, 143.62) * mm, "end": v(-298.37, 144.66) * mm});
            skLineSegment(sketch, "E0.0.691", {"start": v(-298.37, 144.66) * mm, "end": v(-299.76, 145.74) * mm});
            skLineSegment(sketch, "E0.0.692", {"start": v(-299.76, 145.74) * mm, "end": v(-301.14, 146.86) * mm});
            skLineSegment(sketch, "E0.0.693", {"start": v(-301.14, 146.86) * mm, "end": v(-299.77, 151.05) * mm});
            skLineSegment(sketch, "E0.0.694", {"start": v(-299.77, 151.05) * mm, "end": v(-298, 151.14) * mm});
            skLineSegment(sketch, "E0.0.695", {"start": v(-298, 151.14) * mm, "end": v(-296.24, 151.2) * mm});
            skLineSegment(sketch, "E0.0.696", {"start": v(-296.24, 151.2) * mm, "end": v(-294.49, 151.2) * mm});
            skLineSegment(sketch, "E0.0.697", {"start": v(-294.49, 151.2) * mm, "end": v(-293.62, 151.18) * mm});
            skLineSegment(sketch, "E0.0.698", {"start": v(-293.62, 151.18) * mm, "end": v(-293.19, 151.17) * mm});
            skLineSegment(sketch, "E0.0.699", {"start": v(-293.19, 151.17) * mm, "end": v(-292.76, 151.15) * mm});
            skLineSegment(sketch, "E0.0.700", {"start": v(-292.76, 151.15) * mm, "end": v(-291.2, 155.44) * mm});
            skLineSegment(sketch, "E0.0.701", {"start": v(-291.2, 155.44) * mm, "end": v(-291.53, 155.7) * mm});
            skLineSegment(sketch, "E0.0.702", {"start": v(-291.53, 155.7) * mm, "end": v(-291.87, 155.97) * mm});
            skLineSegment(sketch, "E0.0.703", {"start": v(-291.87, 155.97) * mm, "end": v(-292.54, 156.52) * mm});
            skLineSegment(sketch, "E0.0.704", {"start": v(-292.54, 156.52) * mm, "end": v(-293.88, 157.65) * mm});
            skLineSegment(sketch, "E0.0.705", {"start": v(-293.88, 157.65) * mm, "end": v(-295.2, 158.83) * mm});
            skLineSegment(sketch, "E0.0.706", {"start": v(-295.2, 158.83) * mm, "end": v(-296.49, 160.04) * mm});
            skLineSegment(sketch, "E0.0.707", {"start": v(-296.49, 160.04) * mm, "end": v(-294.83, 164.12) * mm});
            skLineSegment(sketch, "E0.0.708", {"start": v(-294.83, 164.12) * mm, "end": v(-293.05, 164.1) * mm});
            skLineSegment(sketch, "E0.0.709", {"start": v(-293.05, 164.1) * mm, "end": v(-291.3, 164.02) * mm});
            skLineSegment(sketch, "E0.0.710", {"start": v(-291.3, 164.02) * mm, "end": v(-289.55, 163.9) * mm});
            skLineSegment(sketch, "E0.0.711", {"start": v(-289.55, 163.9) * mm, "end": v(-288.68, 163.83) * mm});
            skLineSegment(sketch, "E0.0.712", {"start": v(-288.68, 163.83) * mm, "end": v(-288.25, 163.79) * mm});
            skLineSegment(sketch, "E0.0.713", {"start": v(-288.25, 163.79) * mm, "end": v(-287.82, 163.74) * mm});
            skLineSegment(sketch, "E0.0.714", {"start": v(-287.82, 163.74) * mm, "end": v(-285.96, 167.9) * mm});
            skLineSegment(sketch, "E0.0.715", {"start": v(-285.96, 167.9) * mm, "end": v(-286.28, 168.2) * mm});
            skLineSegment(sketch, "E0.0.716", {"start": v(-286.28, 168.2) * mm, "end": v(-286.6, 168.49) * mm});
            skLineSegment(sketch, "E0.0.717", {"start": v(-286.6, 168.49) * mm, "end": v(-287.24, 169.08) * mm});
            skLineSegment(sketch, "E0.0.718", {"start": v(-287.24, 169.08) * mm, "end": v(-288.49, 170.3) * mm});
            skLineSegment(sketch, "E0.0.719", {"start": v(-288.49, 170.3) * mm, "end": v(-289.72, 171.56) * mm});
            skLineSegment(sketch, "E0.0.720", {"start": v(-289.72, 171.56) * mm, "end": v(-290.92, 172.87) * mm});
            skLineSegment(sketch, "E0.0.721", {"start": v(-290.92, 172.87) * mm, "end": v(-288.99, 176.82) * mm});
            skLineSegment(sketch, "E0.0.722", {"start": v(-288.99, 176.82) * mm, "end": v(-287.22, 176.67) * mm});
            skLineSegment(sketch, "E0.0.723", {"start": v(-287.22, 176.67) * mm, "end": v(-285.46, 176.48) * mm});
            skLineSegment(sketch, "E0.0.724", {"start": v(-285.46, 176.48) * mm, "end": v(-283.73, 176.24) * mm});
            skLineSegment(sketch, "E0.0.725", {"start": v(-283.73, 176.24) * mm, "end": v(-282.87, 176.1) * mm});
            skLineSegment(sketch, "E0.0.726", {"start": v(-282.87, 176.1) * mm, "end": v(-282.45, 176.03) * mm});
            skLineSegment(sketch, "E0.0.727", {"start": v(-282.45, 176.03) * mm, "end": v(-282.02, 175.95) * mm});
            skLineSegment(sketch, "E0.0.728", {"start": v(-282.02, 175.95) * mm, "end": v(-279.88, 179.98) * mm});
            skLineSegment(sketch, "E0.0.729", {"start": v(-279.88, 179.98) * mm, "end": v(-280.18, 180.29) * mm});
            skLineSegment(sketch, "E0.0.730", {"start": v(-280.18, 180.29) * mm, "end": v(-280.47, 180.6) * mm});
            skLineSegment(sketch, "E0.0.731", {"start": v(-280.47, 180.6) * mm, "end": v(-281.06, 181.24) * mm});
            skLineSegment(sketch, "E0.0.732", {"start": v(-281.06, 181.24) * mm, "end": v(-282.23, 182.54) * mm});
            skLineSegment(sketch, "E0.0.733", {"start": v(-282.23, 182.54) * mm, "end": v(-283.36, 183.9) * mm});
            skLineSegment(sketch, "E0.0.734", {"start": v(-283.36, 183.9) * mm, "end": v(-284.48, 185.28) * mm});
            skLineSegment(sketch, "E0.0.735", {"start": v(-284.48, 185.28) * mm, "end": v(-282.27, 189.09) * mm});
            skLineSegment(sketch, "E0.0.736", {"start": v(-282.27, 189.09) * mm, "end": v(-280.51, 188.81) * mm});
            skLineSegment(sketch, "E0.0.737", {"start": v(-280.51, 188.81) * mm, "end": v(-278.78, 188.5) * mm});
            skLineSegment(sketch, "E0.0.738", {"start": v(-278.78, 188.5) * mm, "end": v(-277.07, 188.13) * mm});
            skLineSegment(sketch, "E0.0.739", {"start": v(-277.07, 188.13) * mm, "end": v(-276.22, 187.94) * mm});
            skLineSegment(sketch, "E0.0.740", {"start": v(-276.22, 187.94) * mm, "end": v(-275.8, 187.84) * mm});
            skLineSegment(sketch, "E0.0.741", {"start": v(-275.8, 187.84) * mm, "end": v(-275.38, 187.73) * mm});
            skLineSegment(sketch, "E0.0.742", {"start": v(-275.38, 187.73) * mm, "end": v(-272.96, 191.6) * mm});
            skLineSegment(sketch, "E0.0.743", {"start": v(-272.96, 191.6) * mm, "end": v(-273.24, 191.93) * mm});
            skLineSegment(sketch, "E0.0.744", {"start": v(-273.24, 191.93) * mm, "end": v(-273.51, 192.26) * mm});
            skLineSegment(sketch, "E0.0.745", {"start": v(-273.51, 192.26) * mm, "end": v(-274.06, 192.94) * mm});
            skLineSegment(sketch, "E0.0.746", {"start": v(-274.06, 192.94) * mm, "end": v(-275.13, 194.32) * mm});
            skLineSegment(sketch, "E0.0.747", {"start": v(-275.13, 194.32) * mm, "end": v(-276.17, 195.74) * mm});
            skLineSegment(sketch, "E0.0.748", {"start": v(-276.17, 195.74) * mm, "end": v(-277.18, 197.2) * mm});
            skLineSegment(sketch, "E0.0.749", {"start": v(-277.18, 197.2) * mm, "end": v(-274.72, 200.85) * mm});
            skLineSegment(sketch, "E0.0.750", {"start": v(-274.72, 200.85) * mm, "end": v(-272.98, 200.45) * mm});
            skLineSegment(sketch, "E0.0.751", {"start": v(-272.98, 200.45) * mm, "end": v(-271.28, 200.02) * mm});
            skLineSegment(sketch, "E0.0.752", {"start": v(-271.28, 200.02) * mm, "end": v(-269.6, 199.54) * mm});
            skLineSegment(sketch, "E0.0.753", {"start": v(-269.6, 199.54) * mm, "end": v(-268.76, 199.28) * mm});
            skLineSegment(sketch, "E0.0.754", {"start": v(-268.76, 199.28) * mm, "end": v(-268.35, 199.15) * mm});
            skLineSegment(sketch, "E0.0.755", {"start": v(-268.35, 199.15) * mm, "end": v(-267.94, 199.02) * mm});
            skLineSegment(sketch, "E0.0.756", {"start": v(-267.94, 199.02) * mm, "end": v(-265.25, 202.7) * mm});
            skLineSegment(sketch, "E0.0.757", {"start": v(-265.25, 202.7) * mm, "end": v(-265.5, 203.05) * mm});
            skLineSegment(sketch, "E0.0.758", {"start": v(-265.5, 203.05) * mm, "end": v(-265.76, 203.4) * mm});
            skLineSegment(sketch, "E0.0.759", {"start": v(-265.76, 203.4) * mm, "end": v(-266.26, 204.12) * mm});
            skLineSegment(sketch, "E0.0.760", {"start": v(-266.26, 204.12) * mm, "end": v(-267.23, 205.57) * mm});
            skLineSegment(sketch, "E0.0.761", {"start": v(-267.23, 205.57) * mm, "end": v(-268.16, 207.06) * mm});
            skLineSegment(sketch, "E0.0.762", {"start": v(-268.16, 207.06) * mm, "end": v(-269.07, 208.6) * mm});
            skLineSegment(sketch, "E0.0.763", {"start": v(-269.07, 208.6) * mm, "end": v(-266.36, 212.06) * mm});
            skLineSegment(sketch, "E0.0.764", {"start": v(-266.36, 212.06) * mm, "end": v(-264.66, 211.54) * mm});
            skLineSegment(sketch, "E0.0.765", {"start": v(-264.66, 211.54) * mm, "end": v(-262.98, 210.99) * mm});
            skLineSegment(sketch, "E0.0.766", {"start": v(-262.98, 210.99) * mm, "end": v(-261.34, 210.4) * mm});
            skLineSegment(sketch, "E0.0.767", {"start": v(-261.34, 210.4) * mm, "end": v(-260.53, 210.08) * mm});
            skLineSegment(sketch, "E0.0.768", {"start": v(-260.53, 210.08) * mm, "end": v(-260.13, 209.92) * mm});
            skLineSegment(sketch, "E0.0.769", {"start": v(-260.13, 209.92) * mm, "end": v(-259.73, 209.76) * mm});
            skLineSegment(sketch, "E0.0.770", {"start": v(-259.73, 209.76) * mm, "end": v(-256.8, 213.25) * mm});
            skLineSegment(sketch, "E0.0.771", {"start": v(-256.8, 213.25) * mm, "end": v(-257.02, 213.61) * mm});
            skLineSegment(sketch, "E0.0.772", {"start": v(-257.02, 213.61) * mm, "end": v(-257.25, 213.98) * mm});
            skLineSegment(sketch, "E0.0.773", {"start": v(-257.25, 213.98) * mm, "end": v(-257.7, 214.73) * mm});
            skLineSegment(sketch, "E0.0.774", {"start": v(-257.7, 214.73) * mm, "end": v(-258.56, 216.25) * mm});
            skLineSegment(sketch, "E0.0.775", {"start": v(-258.56, 216.25) * mm, "end": v(-259.39, 217.8) * mm});
            skLineSegment(sketch, "E0.0.776", {"start": v(-259.39, 217.8) * mm, "end": v(-260.2, 219.39) * mm});
            skLineSegment(sketch, "E0.0.777", {"start": v(-260.2, 219.39) * mm, "end": v(-257.24, 222.66) * mm});
            skLineSegment(sketch, "E0.0.778", {"start": v(-257.24, 222.66) * mm, "end": v(-255.58, 222.02) * mm});
            skLineSegment(sketch, "E0.0.779", {"start": v(-255.58, 222.02) * mm, "end": v(-253.95, 221.35) * mm});
            skLineSegment(sketch, "E0.0.780", {"start": v(-253.95, 221.35) * mm, "end": v(-252.35, 220.64) * mm});
            skLineSegment(sketch, "E0.0.781", {"start": v(-252.35, 220.64) * mm, "end": v(-251.56, 220.28) * mm});
            skLineSegment(sketch, "E0.0.782", {"start": v(-251.56, 220.28) * mm, "end": v(-251.17, 220.09) * mm});
            skLineSegment(sketch, "E0.0.783", {"start": v(-251.17, 220.09) * mm, "end": v(-250.78, 219.9) * mm});
            skLineSegment(sketch, "E0.0.784", {"start": v(-250.78, 219.9) * mm, "end": v(-247.61, 223.17) * mm});
            skLineSegment(sketch, "E0.0.785", {"start": v(-247.61, 223.17) * mm, "end": v(-247.82, 223.56) * mm});
            skLineSegment(sketch, "E0.0.786", {"start": v(-247.82, 223.56) * mm, "end": v(-248.02, 223.94) * mm});
            skLineSegment(sketch, "E0.0.787", {"start": v(-248.02, 223.94) * mm, "end": v(-248.4, 224.71) * mm});
            skLineSegment(sketch, "E0.0.788", {"start": v(-248.4, 224.71) * mm, "end": v(-249.17, 226.29) * mm});
            skLineSegment(sketch, "E0.0.789", {"start": v(-249.17, 226.29) * mm, "end": v(-249.89, 227.9) * mm});
            skLineSegment(sketch, "E0.0.790", {"start": v(-249.89, 227.9) * mm, "end": v(-250.58, 229.54) * mm});
            skLineSegment(sketch, "E0.0.791", {"start": v(-250.58, 229.54) * mm, "end": v(-247.4, 232.6) * mm});
            skLineSegment(sketch, "E0.0.792", {"start": v(-247.4, 232.6) * mm, "end": v(-245.8, 231.84) * mm});
            skLineSegment(sketch, "E0.0.793", {"start": v(-245.8, 231.84) * mm, "end": v(-244.21, 231.06) * mm});
            skLineSegment(sketch, "E0.0.794", {"start": v(-244.21, 231.06) * mm, "end": v(-242.67, 230.24) * mm});
            skLineSegment(sketch, "E0.0.795", {"start": v(-242.67, 230.24) * mm, "end": v(-241.9, 229.82) * mm});
            skLineSegment(sketch, "E0.0.796", {"start": v(-241.9, 229.82) * mm, "end": v(-241.53, 229.6) * mm});
            skLineSegment(sketch, "E0.0.797", {"start": v(-241.53, 229.6) * mm, "end": v(-241.16, 229.4) * mm});
            skLineSegment(sketch, "E0.0.798", {"start": v(-241.16, 229.4) * mm, "end": v(-237.76, 232.44) * mm});
            skLineSegment(sketch, "E0.0.799", {"start": v(-237.76, 232.44) * mm, "end": v(-237.94, 232.83) * mm});
            skLineSegment(sketch, "E0.0.800", {"start": v(-237.94, 232.83) * mm, "end": v(-238.11, 233.23) * mm});
            skLineSegment(sketch, "E0.0.801", {"start": v(-238.11, 233.23) * mm, "end": v(-238.45, 234.03) * mm});
            skLineSegment(sketch, "E0.0.802", {"start": v(-238.45, 234.03) * mm, "end": v(-239.1, 235.65) * mm});
            skLineSegment(sketch, "E0.0.803", {"start": v(-239.1, 235.65) * mm, "end": v(-239.7, 237.3) * mm});
            skLineSegment(sketch, "E0.0.804", {"start": v(-239.7, 237.3) * mm, "end": v(-240.28, 239) * mm});
            skLineSegment(sketch, "E0.0.805", {"start": v(-240.28, 239) * mm, "end": v(-236.9, 241.82) * mm});
            skLineSegment(sketch, "E0.0.806", {"start": v(-236.9, 241.82) * mm, "end": v(-235.34, 240.96) * mm});
            skLineSegment(sketch, "E0.0.807", {"start": v(-235.34, 240.96) * mm, "end": v(-233.82, 240.07) * mm});
            skLineSegment(sketch, "E0.0.808", {"start": v(-233.82, 240.07) * mm, "end": v(-232.34, 239.14) * mm});
            skLineSegment(sketch, "E0.0.809", {"start": v(-232.34, 239.14) * mm, "end": v(-231.6, 238.67) * mm});
            skLineSegment(sketch, "E0.0.810", {"start": v(-231.6, 238.67) * mm, "end": v(-231.25, 238.43) * mm});
            skLineSegment(sketch, "E0.0.811", {"start": v(-231.25, 238.43) * mm, "end": v(-230.9, 238.19) * mm});
            skLineSegment(sketch, "E0.0.812", {"start": v(-230.9, 238.19) * mm, "end": v(-227.3, 241) * mm});
            skLineSegment(sketch, "E0.0.813", {"start": v(-227.3, 241) * mm, "end": v(-227.44, 241.4) * mm});
            skLineSegment(sketch, "E0.0.814", {"start": v(-227.44, 241.4) * mm, "end": v(-227.59, 241.8) * mm});
            skLineSegment(sketch, "E0.0.815", {"start": v(-227.59, 241.8) * mm, "end": v(-227.87, 242.63) * mm});
            skLineSegment(sketch, "E0.0.816", {"start": v(-227.87, 242.63) * mm, "end": v(-228.4, 244.3) * mm});
            skLineSegment(sketch, "E0.0.817", {"start": v(-228.4, 244.3) * mm, "end": v(-228.89, 245.99) * mm});
            skLineSegment(sketch, "E0.0.818", {"start": v(-228.89, 245.99) * mm, "end": v(-229.34, 247.7) * mm});
            skLineSegment(sketch, "E0.0.819", {"start": v(-229.34, 247.7) * mm, "end": v(-225.78, 250.29) * mm});
            skLineSegment(sketch, "E0.0.820", {"start": v(-225.78, 250.29) * mm, "end": v(-224.28, 249.32) * mm});
            skLineSegment(sketch, "E0.0.821", {"start": v(-224.28, 249.32) * mm, "end": v(-222.83, 248.33) * mm});
            skLineSegment(sketch, "E0.0.822", {"start": v(-222.83, 248.33) * mm, "end": v(-221.41, 247.3) * mm});
            skLineSegment(sketch, "E0.0.823", {"start": v(-221.41, 247.3) * mm, "end": v(-220.72, 246.78) * mm});
            skLineSegment(sketch, "E0.0.824", {"start": v(-220.72, 246.78) * mm, "end": v(-220.38, 246.51) * mm});
            skLineSegment(sketch, "E0.0.825", {"start": v(-220.38, 246.51) * mm, "end": v(-220.04, 246.25) * mm});
            skLineSegment(sketch, "E0.0.826", {"start": v(-220.04, 246.25) * mm, "end": v(-216.25, 248.8) * mm});
            skLineSegment(sketch, "E0.0.827", {"start": v(-216.25, 248.8) * mm, "end": v(-216.37, 249.2) * mm});
            skLineSegment(sketch, "E0.0.828", {"start": v(-216.37, 249.2) * mm, "end": v(-216.49, 249.63) * mm});
            skLineSegment(sketch, "E0.0.829", {"start": v(-216.49, 249.63) * mm, "end": v(-216.7, 250.46) * mm});
            skLineSegment(sketch, "E0.0.830", {"start": v(-216.7, 250.46) * mm, "end": v(-217.12, 252.16) * mm});
            skLineSegment(sketch, "E0.0.831", {"start": v(-217.12, 252.16) * mm, "end": v(-217.5, 253.89) * mm});
            skLineSegment(sketch, "E0.0.832", {"start": v(-217.5, 253.89) * mm, "end": v(-217.83, 255.63) * mm});
            skLineSegment(sketch, "E0.0.833", {"start": v(-217.83, 255.63) * mm, "end": v(-214.1, 257.96) * mm});
            skLineSegment(sketch, "E0.0.834", {"start": v(-214.1, 257.96) * mm, "end": v(-212.67, 256.9) * mm});
            skLineSegment(sketch, "E0.0.835", {"start": v(-212.67, 256.9) * mm, "end": v(-211.29, 255.8) * mm});
            skLineSegment(sketch, "E0.0.836", {"start": v(-211.29, 255.8) * mm, "end": v(-209.94, 254.68) * mm});
            skLineSegment(sketch, "E0.0.837", {"start": v(-209.94, 254.68) * mm, "end": v(-209.29, 254.1) * mm});
            skLineSegment(sketch, "E0.0.838", {"start": v(-209.29, 254.1) * mm, "end": v(-208.97, 253.82) * mm});
            skLineSegment(sketch, "E0.0.839", {"start": v(-208.97, 253.82) * mm, "end": v(-208.64, 253.53) * mm});
            skLineSegment(sketch, "E0.0.840", {"start": v(-208.64, 253.53) * mm, "end": v(-204.7, 255.8) * mm});
            skLineSegment(sketch, "E0.0.841", {"start": v(-204.7, 255.8) * mm, "end": v(-204.78, 256.23) * mm});
            skLineSegment(sketch, "E0.0.842", {"start": v(-204.78, 256.23) * mm, "end": v(-204.87, 256.65) * mm});
            skLineSegment(sketch, "E0.0.843", {"start": v(-204.87, 256.65) * mm, "end": v(-205.03, 257.5) * mm});
            skLineSegment(sketch, "E0.0.844", {"start": v(-205.03, 257.5) * mm, "end": v(-205.33, 259.23) * mm});
            skLineSegment(sketch, "E0.0.845", {"start": v(-205.33, 259.23) * mm, "end": v(-205.58, 260.97) * mm});
            skLineSegment(sketch, "E0.0.846", {"start": v(-205.58, 260.97) * mm, "end": v(-205.79, 262.74) * mm});
            skLineSegment(sketch, "E0.0.847", {"start": v(-205.79, 262.74) * mm, "end": v(-201.9, 264.8) * mm});
            skLineSegment(sketch, "E0.0.848", {"start": v(-201.9, 264.8) * mm, "end": v(-200.55, 263.64) * mm});
            skLineSegment(sketch, "E0.0.849", {"start": v(-200.55, 263.64) * mm, "end": v(-199.25, 262.45) * mm});
            skLineSegment(sketch, "E0.0.850", {"start": v(-199.25, 262.45) * mm, "end": v(-198, 261.24) * mm});
            skLineSegment(sketch, "E0.0.851", {"start": v(-198, 261.24) * mm, "end": v(-197.38, 260.62) * mm});
            skLineSegment(sketch, "E0.0.852", {"start": v(-197.38, 260.62) * mm, "end": v(-197.07, 260.31) * mm});
            skLineSegment(sketch, "E0.0.853", {"start": v(-197.07, 260.31) * mm, "end": v(-196.77, 260) * mm});
            skLineSegment(sketch, "E0.0.854", {"start": v(-196.77, 260) * mm, "end": v(-192.67, 262) * mm});
            skLineSegment(sketch, "E0.0.855", {"start": v(-192.67, 262) * mm, "end": v(-192.73, 262.42) * mm});
            skLineSegment(sketch, "E0.0.856", {"start": v(-192.73, 262.42) * mm, "end": v(-192.79, 262.85) * mm});
            skLineSegment(sketch, "E0.0.857", {"start": v(-192.79, 262.85) * mm, "end": v(-192.9, 263.71) * mm});
            skLineSegment(sketch, "E0.0.858", {"start": v(-192.9, 263.71) * mm, "end": v(-193.07, 265.45) * mm});
            skLineSegment(sketch, "E0.0.859", {"start": v(-193.07, 265.45) * mm, "end": v(-193.2, 267.21) * mm});
            skLineSegment(sketch, "E0.0.860", {"start": v(-193.2, 267.21) * mm, "end": v(-193.28, 268.99) * mm});
            skLineSegment(sketch, "E0.0.861", {"start": v(-193.28, 268.99) * mm, "end": v(-189.26, 270.77) * mm});
            skLineSegment(sketch, "E0.0.862", {"start": v(-189.26, 270.77) * mm, "end": v(-188, 269.52) * mm});
            skLineSegment(sketch, "E0.0.863", {"start": v(-188, 269.52) * mm, "end": v(-186.78, 268.24) * mm});
            skLineSegment(sketch, "E0.0.864", {"start": v(-186.78, 268.24) * mm, "end": v(-185.6, 266.95) * mm});
            skLineSegment(sketch, "E0.0.865", {"start": v(-185.6, 266.95) * mm, "end": v(-185.04, 266.3) * mm});
            skLineSegment(sketch, "E0.0.866", {"start": v(-185.04, 266.3) * mm, "end": v(-184.76, 265.96) * mm});
            skLineSegment(sketch, "E0.0.867", {"start": v(-184.76, 265.96) * mm, "end": v(-184.48, 265.63) * mm});
            skLineSegment(sketch, "E0.0.868", {"start": v(-184.48, 265.63) * mm, "end": v(-180.25, 267.33) * mm});
            skLineSegment(sketch, "E0.0.869", {"start": v(-180.25, 267.33) * mm, "end": v(-180.28, 267.76) * mm});
            skLineSegment(sketch, "E0.0.870", {"start": v(-180.28, 267.76) * mm, "end": v(-180.3, 268.2) * mm});
            skLineSegment(sketch, "E0.0.871", {"start": v(-180.3, 268.2) * mm, "end": v(-180.35, 269.06) * mm});
            skLineSegment(sketch, "E0.0.872", {"start": v(-180.35, 269.06) * mm, "end": v(-180.4, 270.8) * mm});
            skLineSegment(sketch, "E0.0.873", {"start": v(-180.4, 270.8) * mm, "end": v(-180.4, 272.57) * mm});
            skLineSegment(sketch, "E0.0.874", {"start": v(-180.4, 272.57) * mm, "end": v(-180.37, 274.35) * mm});
            skLineSegment(sketch, "E0.0.875", {"start": v(-180.37, 274.35) * mm, "end": v(-176.23, 275.85) * mm});
            skLineSegment(sketch, "E0.0.876", {"start": v(-176.23, 275.85) * mm, "end": v(-175.06, 274.5) * mm});
            skLineSegment(sketch, "E0.0.877", {"start": v(-175.06, 274.5) * mm, "end": v(-173.94, 273.15) * mm});
            skLineSegment(sketch, "E0.0.878", {"start": v(-173.94, 273.15) * mm, "end": v(-172.86, 271.78) * mm});
            skLineSegment(sketch, "E0.0.879", {"start": v(-172.86, 271.78) * mm, "end": v(-172.33, 271.08) * mm});
            skLineSegment(sketch, "E0.0.880", {"start": v(-172.33, 271.08) * mm, "end": v(-172.08, 270.73) * mm});
            skLineSegment(sketch, "E0.0.881", {"start": v(-172.08, 270.73) * mm, "end": v(-171.82, 270.39) * mm});
            skLineSegment(sketch, "E0.0.882", {"start": v(-171.82, 270.39) * mm, "end": v(-167.49, 271.79) * mm});
            skLineSegment(sketch, "E0.0.883", {"start": v(-167.49, 271.79) * mm, "end": v(-167.49, 272.22) * mm});
            skLineSegment(sketch, "E0.0.884", {"start": v(-167.49, 272.22) * mm, "end": v(-167.48, 272.65) * mm});
            skLineSegment(sketch, "E0.0.885", {"start": v(-167.48, 272.65) * mm, "end": v(-167.46, 273.52) * mm});
            skLineSegment(sketch, "E0.0.886", {"start": v(-167.46, 273.52) * mm, "end": v(-167.4, 275.27) * mm});
            skLineSegment(sketch, "E0.0.887", {"start": v(-167.4, 275.27) * mm, "end": v(-167.28, 277.03) * mm});
            skLineSegment(sketch, "E0.0.888", {"start": v(-167.28, 277.03) * mm, "end": v(-167.12, 278.8) * mm});
            skLineSegment(sketch, "E0.0.889", {"start": v(-167.12, 278.8) * mm, "end": v(-162.88, 280) * mm});
            skLineSegment(sketch, "E0.0.890", {"start": v(-162.88, 280) * mm, "end": v(-161.8, 278.59) * mm});
            skLineSegment(sketch, "E0.0.891", {"start": v(-161.8, 278.59) * mm, "end": v(-160.78, 277.15) * mm});
            skLineSegment(sketch, "E0.0.892", {"start": v(-160.78, 277.15) * mm, "end": v(-159.8, 275.7) * mm});
            skLineSegment(sketch, "E0.0.893", {"start": v(-159.8, 275.7) * mm, "end": v(-159.33, 274.98) * mm});
            skLineSegment(sketch, "E0.0.894", {"start": v(-159.33, 274.98) * mm, "end": v(-159.1, 274.61) * mm});
            skLineSegment(sketch, "E0.0.895", {"start": v(-159.1, 274.61) * mm, "end": v(-158.87, 274.25) * mm});
            skLineSegment(sketch, "E0.0.896", {"start": v(-158.87, 274.25) * mm, "end": v(-154.44, 275.34) * mm});
            skLineSegment(sketch, "E0.0.897", {"start": v(-154.44, 275.34) * mm, "end": v(-154.41, 275.77) * mm});
            skLineSegment(sketch, "E0.0.898", {"start": v(-154.41, 275.77) * mm, "end": v(-154.38, 276.2) * mm});
            skLineSegment(sketch, "E0.0.899", {"start": v(-154.38, 276.2) * mm, "end": v(-154.3, 277.07) * mm});
            skLineSegment(sketch, "E0.0.900", {"start": v(-154.3, 277.07) * mm, "end": v(-154.1, 278.8) * mm});
            skLineSegment(sketch, "E0.0.901", {"start": v(-154.1, 278.8) * mm, "end": v(-153.87, 280.55) * mm});
            skLineSegment(sketch, "E0.0.902", {"start": v(-153.87, 280.55) * mm, "end": v(-153.58, 282.3) * mm});
            skLineSegment(sketch, "E0.0.903", {"start": v(-153.58, 282.3) * mm, "end": v(-149.27, 283.22) * mm});
            skLineSegment(sketch, "E0.0.904", {"start": v(-149.27, 283.22) * mm, "end": v(-148.3, 281.73) * mm});
            skLineSegment(sketch, "E0.0.905", {"start": v(-148.3, 281.73) * mm, "end": v(-147.38, 280.23) * mm});
            skLineSegment(sketch, "E0.0.906", {"start": v(-147.38, 280.23) * mm, "end": v(-146.5, 278.72) * mm});
            skLineSegment(sketch, "E0.0.907", {"start": v(-146.5, 278.72) * mm, "end": v(-146.08, 277.96) * mm});
            skLineSegment(sketch, "E0.0.908", {"start": v(-146.08, 277.96) * mm, "end": v(-145.87, 277.58) * mm});
            skLineSegment(sketch, "E0.0.909", {"start": v(-145.87, 277.58) * mm, "end": v(-145.67, 277.2) * mm});
            skLineSegment(sketch, "E0.0.910", {"start": v(-145.67, 277.2) * mm, "end": v(-141.18, 277.98) * mm});
            skLineSegment(sketch, "E0.0.911", {"start": v(-141.18, 277.98) * mm, "end": v(-141.12, 278.4) * mm});
            skLineSegment(sketch, "E0.0.912", {"start": v(-141.12, 278.4) * mm, "end": v(-141.06, 278.84) * mm});
            skLineSegment(sketch, "E0.0.913", {"start": v(-141.06, 278.84) * mm, "end": v(-140.92, 279.7) * mm});
            skLineSegment(sketch, "E0.0.914", {"start": v(-140.92, 279.7) * mm, "end": v(-140.6, 281.41) * mm});
            skLineSegment(sketch, "E0.0.915", {"start": v(-140.6, 281.41) * mm, "end": v(-140.25, 283.14) * mm});
            skLineSegment(sketch, "E0.0.916", {"start": v(-140.25, 283.14) * mm, "end": v(-139.84, 284.87) * mm});
            skLineSegment(sketch, "E0.0.917", {"start": v(-139.84, 284.87) * mm, "end": v(-135.48, 285.48) * mm});
            skLineSegment(sketch, "E0.0.918", {"start": v(-135.48, 285.48) * mm, "end": v(-134.61, 283.92) * mm});
            skLineSegment(sketch, "E0.0.919", {"start": v(-134.61, 283.92) * mm, "end": v(-133.8, 282.36) * mm});
            skLineSegment(sketch, "E0.0.920", {"start": v(-133.8, 282.36) * mm, "end": v(-133.02, 280.8) * mm});
            skLineSegment(sketch, "E0.0.921", {"start": v(-133.02, 280.8) * mm, "end": v(-132.66, 280) * mm});
            skLineSegment(sketch, "E0.0.922", {"start": v(-132.66, 280) * mm, "end": v(-132.48, 279.6) * mm});
            skLineSegment(sketch, "E0.0.923", {"start": v(-132.48, 279.6) * mm, "end": v(-132.3, 279.21) * mm});
            skLineSegment(sketch, "E0.0.924", {"start": v(-132.3, 279.21) * mm, "end": v(-127.77, 279.68) * mm});
            skLineSegment(sketch, "E0.0.925", {"start": v(-127.77, 279.68) * mm, "end": v(-127.68, 280.1) * mm});
            skLineSegment(sketch, "E0.0.926", {"start": v(-127.68, 280.1) * mm, "end": v(-127.59, 280.53) * mm});
            skLineSegment(sketch, "E0.0.927", {"start": v(-127.59, 280.53) * mm, "end": v(-127.39, 281.38) * mm});
            skLineSegment(sketch, "E0.0.928", {"start": v(-127.39, 281.38) * mm, "end": v(-126.96, 283.07) * mm});
            skLineSegment(sketch, "E0.0.929", {"start": v(-126.96, 283.07) * mm, "end": v(-126.48, 284.77) * mm});
            skLineSegment(sketch, "E0.0.930", {"start": v(-126.48, 284.77) * mm, "end": v(-125.95, 286.46) * mm});
            skLineSegment(sketch, "E0.0.931", {"start": v(-125.95, 286.46) * mm, "end": v(-121.56, 286.76) * mm});
            skLineSegment(sketch, "E0.0.932", {"start": v(-121.56, 286.76) * mm, "end": v(-120.8, 285.15) * mm});
            skLineSegment(sketch, "E0.0.933", {"start": v(-120.8, 285.15) * mm, "end": v(-120.1, 283.54) * mm});
            skLineSegment(sketch, "E0.0.934", {"start": v(-120.1, 283.54) * mm, "end": v(-119.44, 281.92) * mm});
            skLineSegment(sketch, "E0.0.935", {"start": v(-119.44, 281.92) * mm, "end": v(-119.13, 281.1) * mm});
            skLineSegment(sketch, "E0.0.936", {"start": v(-119.13, 281.1) * mm, "end": v(-118.97, 280.7) * mm});
            skLineSegment(sketch, "E0.0.937", {"start": v(-118.97, 280.7) * mm, "end": v(-118.83, 280.3) * mm});
            skLineSegment(sketch, "E0.0.938", {"start": v(-118.83, 280.3) * mm, "end": v(-114.27, 280.45) * mm});
            skLineSegment(sketch, "E0.0.939", {"start": v(-114.27, 280.45) * mm, "end": v(-114.15, 280.87) * mm});
            skLineSegment(sketch, "E0.0.940", {"start": v(-114.15, 280.87) * mm, "end": v(-114.03, 281.28) * mm});
            skLineSegment(sketch, "E0.0.941", {"start": v(-114.03, 281.28) * mm, "end": v(-113.77, 282.11) * mm});
            skLineSegment(sketch, "E0.0.942", {"start": v(-113.77, 282.11) * mm, "end": v(-113.22, 283.77) * mm});
            skLineSegment(sketch, "E0.0.943", {"start": v(-113.22, 283.77) * mm, "end": v(-112.63, 285.43) * mm});
            skLineSegment(sketch, "E0.0.944", {"start": v(-112.63, 285.43) * mm, "end": v(-111.98, 287.09) * mm});
            skLineSegment(sketch, "E0.0.945", {"start": v(-111.98, 287.09) * mm, "end": v(-107.58, 287.08) * mm});
            skLineSegment(sketch, "E0.0.946", {"start": v(-107.58, 287.08) * mm, "end": v(-106.94, 285.42) * mm});
            skLineSegment(sketch, "E0.0.947", {"start": v(-106.94, 285.42) * mm, "end": v(-106.35, 283.76) * mm});
            skLineSegment(sketch, "E0.0.948", {"start": v(-106.35, 283.76) * mm, "end": v(-105.8, 282.1) * mm});
            skLineSegment(sketch, "E0.0.949", {"start": v(-105.8, 282.1) * mm, "end": v(-105.55, 281.27) * mm});
            skLineSegment(sketch, "E0.0.950", {"start": v(-105.55, 281.27) * mm, "end": v(-105.43, 280.85) * mm});
            skLineSegment(sketch, "E0.0.951", {"start": v(-105.43, 280.85) * mm, "end": v(-105.3, 280.44) * mm});
            skLineSegment(sketch, "E0.0.952", {"start": v(-105.3, 280.44) * mm, "end": v(-100.75, 280.27) * mm});
            skLineSegment(sketch, "E0.0.953", {"start": v(-100.75, 280.27) * mm, "end": v(-100.6, 280.68) * mm});
            skLineSegment(sketch, "E0.0.954", {"start": v(-100.6, 280.68) * mm, "end": v(-100.45, 281.08) * mm});
            skLineSegment(sketch, "E0.0.955", {"start": v(-100.45, 281.08) * mm, "end": v(-100.14, 281.9) * mm});
            skLineSegment(sketch, "E0.0.956", {"start": v(-100.14, 281.9) * mm, "end": v(-99.48, 283.51) * mm});
            skLineSegment(sketch, "E0.0.957", {"start": v(-99.48, 283.51) * mm, "end": v(-98.76, 285.12) * mm});
            skLineSegment(sketch, "E0.0.958", {"start": v(-98.76, 285.12) * mm, "end": v(-98, 286.73) * mm});
            skLineSegment(sketch, "E0.0.959", {"start": v(-98, 286.73) * mm, "end": v(-93.61, 286.42) * mm});
            skLineSegment(sketch, "E0.0.960", {"start": v(-93.61, 286.42) * mm, "end": v(-93.1, 284.72) * mm});
            skLineSegment(sketch, "E0.0.961", {"start": v(-93.1, 284.72) * mm, "end": v(-92.62, 283.02) * mm});
            skLineSegment(sketch, "E0.0.962", {"start": v(-92.62, 283.02) * mm, "end": v(-92.19, 281.33) * mm});
            skLineSegment(sketch, "E0.0.963", {"start": v(-92.19, 281.33) * mm, "end": v(-92, 280.48) * mm});
            skLineSegment(sketch, "E0.0.964", {"start": v(-92, 280.48) * mm, "end": v(-91.9, 280.06) * mm});
            skLineSegment(sketch, "E0.0.965", {"start": v(-91.9, 280.06) * mm, "end": v(-91.81, 279.63) * mm});
            skLineSegment(sketch, "E0.0.966", {"start": v(-91.81, 279.63) * mm, "end": v(-87.28, 279.15) * mm});
            skLineSegment(sketch, "E0.0.967", {"start": v(-87.28, 279.15) * mm, "end": v(-87.1, 279.55) * mm});
            skLineSegment(sketch, "E0.0.968", {"start": v(-87.1, 279.55) * mm, "end": v(-86.92, 279.94) * mm});
            skLineSegment(sketch, "E0.0.969", {"start": v(-86.92, 279.94) * mm, "end": v(-86.55, 280.73) * mm});
            skLineSegment(sketch, "E0.0.970", {"start": v(-86.55, 280.73) * mm, "end": v(-85.78, 282.3) * mm});
            skLineSegment(sketch, "E0.0.971", {"start": v(-85.78, 282.3) * mm, "end": v(-84.96, 283.85) * mm});
            skLineSegment(sketch, "E0.0.972", {"start": v(-84.96, 283.85) * mm, "end": v(-84.09, 285.4) * mm});
            skLineSegment(sketch, "E0.0.973", {"start": v(-84.09, 285.4) * mm, "end": v(-79.73, 284.79) * mm});
            skLineSegment(sketch, "E0.0.974", {"start": v(-79.73, 284.79) * mm, "end": v(-79.33, 283.05) * mm});
            skLineSegment(sketch, "E0.0.975", {"start": v(-79.33, 283.05) * mm, "end": v(-78.97, 281.33) * mm});
            skLineSegment(sketch, "E0.0.976", {"start": v(-78.97, 281.33) * mm, "end": v(-78.66, 279.6) * mm});
            skLineSegment(sketch, "E0.0.977", {"start": v(-78.66, 279.6) * mm, "end": v(-78.53, 278.75) * mm});
            skLineSegment(sketch, "E0.0.978", {"start": v(-78.53, 278.75) * mm, "end": v(-78.46, 278.32) * mm});
            skLineSegment(sketch, "E0.0.979", {"start": v(-78.46, 278.32) * mm, "end": v(-78.4, 277.9) * mm});
            skLineSegment(sketch, "E0.0.980", {"start": v(-78.4, 277.9) * mm, "end": v(-73.92, 277.1) * mm});
            skLineSegment(sketch, "E0.0.981", {"start": v(-73.92, 277.1) * mm, "end": v(-73.71, 277.48) * mm});
            skLineSegment(sketch, "E0.0.982", {"start": v(-73.71, 277.48) * mm, "end": v(-73.5, 277.86) * mm});
            skLineSegment(sketch, "E0.0.983", {"start": v(-73.5, 277.86) * mm, "end": v(-73.08, 278.61) * mm});
            skLineSegment(sketch, "E0.0.984", {"start": v(-73.08, 278.61) * mm, "end": v(-72.2, 280.12) * mm});
            skLineSegment(sketch, "E0.0.985", {"start": v(-72.2, 280.12) * mm, "end": v(-71.27, 281.62) * mm});
            skLineSegment(sketch, "E0.0.986", {"start": v(-71.27, 281.62) * mm, "end": v(-70.3, 283.1) * mm});
            skLineSegment(sketch, "E0.0.987", {"start": v(-70.3, 283.1) * mm, "end": v(-66, 282.19) * mm});
            skLineSegment(sketch, "E0.0.988", {"start": v(-66, 282.19) * mm, "end": v(-65.71, 280.43) * mm});
            skLineSegment(sketch, "E0.0.989", {"start": v(-65.71, 280.43) * mm, "end": v(-65.48, 278.68) * mm});
            skLineSegment(sketch, "E0.0.990", {"start": v(-65.48, 278.68) * mm, "end": v(-65.29, 276.95) * mm});
            skLineSegment(sketch, "E0.0.991", {"start": v(-65.29, 276.95) * mm, "end": v(-65.21, 276.08) * mm});
            skLineSegment(sketch, "E0.0.992", {"start": v(-65.21, 276.08) * mm, "end": v(-65.18, 275.65) * mm});
            skLineSegment(sketch, "E0.0.993", {"start": v(-65.18, 275.65) * mm, "end": v(-65.15, 275.22) * mm});
            skLineSegment(sketch, "E0.0.994", {"start": v(-65.15, 275.22) * mm, "end": v(-60.73, 274.1) * mm});
            skLineSegment(sketch, "E0.0.995", {"start": v(-60.73, 274.1) * mm, "end": v(-60.5, 274.48) * mm});
            skLineSegment(sketch, "E0.0.996", {"start": v(-60.5, 274.48) * mm, "end": v(-60.27, 274.84) * mm});
            skLineSegment(sketch, "E0.0.997", {"start": v(-60.27, 274.84) * mm, "end": v(-59.8, 275.57) * mm});
            skLineSegment(sketch, "E0.0.998", {"start": v(-59.8, 275.57) * mm, "end": v(-58.8, 277.01) * mm});
            skLineSegment(sketch, "E0.0.999", {"start": v(-58.8, 277.01) * mm, "end": v(-57.78, 278.44) * mm});
            skLineSegment(sketch, "E0.0.1000", {"start": v(-57.78, 278.44) * mm, "end": v(-56.7, 279.86) * mm});
            skLineSegment(sketch, "E0.0.1001", {"start": v(-56.7, 279.86) * mm, "end": v(-52.47, 278.64) * mm});
            skLineSegment(sketch, "E0.0.1002", {"start": v(-52.47, 278.64) * mm, "end": v(-52.31, 276.87) * mm});
            skLineSegment(sketch, "E0.0.1003", {"start": v(-52.31, 276.87) * mm, "end": v(-52.2, 275.1) * mm});
            skLineSegment(sketch, "E0.0.1004", {"start": v(-52.2, 275.1) * mm, "end": v(-52.13, 273.36) * mm});
            skLineSegment(sketch, "E0.0.1005", {"start": v(-52.13, 273.36) * mm, "end": v(-52.12, 272.5) * mm});
            skLineSegment(sketch, "E0.0.1006", {"start": v(-52.12, 272.5) * mm, "end": v(-52.12, 272.06) * mm});
            skLineSegment(sketch, "E0.0.1007", {"start": v(-52.12, 272.06) * mm, "end": v(-52.12, 271.63) * mm});
            skLineSegment(sketch, "E0.0.1008", {"start": v(-52.12, 271.63) * mm, "end": v(-47.78, 270.21) * mm});
            skLineSegment(sketch, "E0.0.1009", {"start": v(-47.78, 270.21) * mm, "end": v(-47.53, 270.56) * mm});
            skLineSegment(sketch, "E0.0.1010", {"start": v(-47.53, 270.56) * mm, "end": v(-47.27, 270.9) * mm});
            skLineSegment(sketch, "E0.0.1011", {"start": v(-47.27, 270.9) * mm, "end": v(-46.75, 271.6) * mm});
            skLineSegment(sketch, "E0.0.1012", {"start": v(-46.75, 271.6) * mm, "end": v(-45.66, 272.97) * mm});
            skLineSegment(sketch, "E0.0.1013", {"start": v(-45.66, 272.97) * mm, "end": v(-44.53, 274.33) * mm});
            skLineSegment(sketch, "E0.0.1014", {"start": v(-44.53, 274.33) * mm, "end": v(-43.36, 275.66) * mm});
            skLineSegment(sketch, "E0.0.1015", {"start": v(-43.36, 275.66) * mm, "end": v(-39.23, 274.15) * mm});
            skLineSegment(sketch, "E0.0.1016", {"start": v(-39.23, 274.15) * mm, "end": v(-39.2, 272.37) * mm});
            skLineSegment(sketch, "E0.0.1017", {"start": v(-39.2, 272.37) * mm, "end": v(-39.2, 270.61) * mm});
            skLineSegment(sketch, "E0.0.1018", {"start": v(-39.2, 270.61) * mm, "end": v(-39.26, 268.86) * mm});
            skLineSegment(sketch, "E0.0.1019", {"start": v(-39.26, 268.86) * mm, "end": v(-39.3, 268) * mm});
            skLineSegment(sketch, "E0.0.1020", {"start": v(-39.3, 268) * mm, "end": v(-39.33, 267.57) * mm});
            skLineSegment(sketch, "E0.0.1021", {"start": v(-39.33, 267.57) * mm, "end": v(-39.37, 267.13) * mm});
            skLineSegment(sketch, "E0.0.1022", {"start": v(-39.37, 267.13) * mm, "end": v(-35.14, 265.42) * mm});
            skLineSegment(sketch, "E0.0.1023", {"start": v(-35.14, 265.42) * mm, "end": v(-34.86, 265.75) * mm});
            skLineSegment(sketch, "E0.0.1024", {"start": v(-34.86, 265.75) * mm, "end": v(-34.58, 266.08) * mm});
            skLineSegment(sketch, "E0.0.1025", {"start": v(-34.58, 266.08) * mm, "end": v(-34, 266.73) * mm});
            skLineSegment(sketch, "E0.0.1026", {"start": v(-34, 266.73) * mm, "end": v(-32.83, 268.03) * mm});
            skLineSegment(sketch, "E0.0.1027", {"start": v(-32.83, 268.03) * mm, "end": v(-31.61, 269.3) * mm});
            skLineSegment(sketch, "E0.0.1028", {"start": v(-31.61, 269.3) * mm, "end": v(-30.35, 270.55) * mm});
            skLineSegment(sketch, "E0.0.1029", {"start": v(-30.35, 270.55) * mm, "end": v(-26.33, 268.75) * mm});
            skLineSegment(sketch, "E0.0.1030", {"start": v(-26.33, 268.75) * mm, "end": v(-26.42, 266.98) * mm});
            skLineSegment(sketch, "E0.0.1031", {"start": v(-26.42, 266.98) * mm, "end": v(-26.56, 265.22) * mm});
            skLineSegment(sketch, "E0.0.1032", {"start": v(-26.56, 265.22) * mm, "end": v(-26.73, 263.48) * mm});
            skLineSegment(sketch, "E0.0.1033", {"start": v(-26.73, 263.48) * mm, "end": v(-26.84, 262.62) * mm});
            skLineSegment(sketch, "E0.0.1034", {"start": v(-26.84, 262.62) * mm, "end": v(-26.9, 262.2) * mm});
            skLineSegment(sketch, "E0.0.1035", {"start": v(-26.9, 262.2) * mm, "end": v(-26.96, 261.76) * mm});
            skLineSegment(sketch, "E0.0.1036", {"start": v(-26.96, 261.76) * mm, "end": v(-22.86, 259.76) * mm});
            skLineSegment(sketch, "E0.0.1037", {"start": v(-22.86, 259.76) * mm, "end": v(-22.56, 260.07) * mm});
            skLineSegment(sketch, "E0.0.1038", {"start": v(-22.56, 260.07) * mm, "end": v(-22.26, 260.38) * mm});
            skLineSegment(sketch, "E0.0.1039", {"start": v(-22.26, 260.38) * mm, "end": v(-21.64, 261) * mm});
            skLineSegment(sketch, "E0.0.1040", {"start": v(-21.64, 261) * mm, "end": v(-20.38, 262.2) * mm});
            skLineSegment(sketch, "E0.0.1041", {"start": v(-20.38, 262.2) * mm, "end": v(-19.07, 263.38) * mm});
            skLineSegment(sketch, "E0.0.1042", {"start": v(-19.07, 263.38) * mm, "end": v(-17.73, 264.54) * mm});
            skLineSegment(sketch, "E0.0.1043", {"start": v(-17.73, 264.54) * mm, "end": v(-13.84, 262.47) * mm});
            skLineSegment(sketch, "E0.0.1044", {"start": v(-13.84, 262.47) * mm, "end": v(-14.06, 260.7) * mm});
            skLineSegment(sketch, "E0.0.1045", {"start": v(-14.06, 260.7) * mm, "end": v(-14.31, 258.96) * mm});
            skLineSegment(sketch, "E0.0.1046", {"start": v(-14.31, 258.96) * mm, "end": v(-14.61, 257.24) * mm});
            skLineSegment(sketch, "E0.0.1047", {"start": v(-14.61, 257.24) * mm, "end": v(-14.78, 256.39) * mm});
            skLineSegment(sketch, "E0.0.1048", {"start": v(-14.78, 256.39) * mm, "end": v(-14.86, 255.96) * mm});
            skLineSegment(sketch, "E0.0.1049", {"start": v(-14.86, 255.96) * mm, "end": v(-14.95, 255.54) * mm});
            skLineSegment(sketch, "E0.0.1050", {"start": v(-14.95, 255.54) * mm, "end": v(-11, 253.26) * mm});
            skLineSegment(sketch, "E0.0.1051", {"start": v(-11, 253.26) * mm, "end": v(-10.69, 253.54) * mm});
            skLineSegment(sketch, "E0.0.1052", {"start": v(-10.69, 253.54) * mm, "end": v(-10.36, 253.83) * mm});
            skLineSegment(sketch, "E0.0.1053", {"start": v(-10.36, 253.83) * mm, "end": v(-9.7, 254.4) * mm});
            skLineSegment(sketch, "E0.0.1054", {"start": v(-9.7, 254.4) * mm, "end": v(-8.36, 255.52) * mm});
            skLineSegment(sketch, "E0.0.1055", {"start": v(-8.36, 255.52) * mm, "end": v(-6.98, 256.6) * mm});
            skLineSegment(sketch, "E0.0.1056", {"start": v(-6.98, 256.6) * mm, "end": v(-5.55, 257.67) * mm});
            skLineSegment(sketch, "E0.0.1057", {"start": v(-5.55, 257.67) * mm, "end": v(-1.82, 255.33) * mm});
            skLineSegment(sketch, "E0.0.1058", {"start": v(-1.82, 255.33) * mm, "end": v(-2.16, 253.59) * mm});
            skLineSegment(sketch, "E0.0.1059", {"start": v(-2.16, 253.59) * mm, "end": v(-2.54, 251.86) * mm});
            skLineSegment(sketch, "E0.0.1060", {"start": v(-2.54, 251.86) * mm, "end": v(-2.95, 250.17) * mm});
            skLineSegment(sketch, "E0.0.1061", {"start": v(-2.95, 250.17) * mm, "end": v(-3.18, 249.33) * mm});
            skLineSegment(sketch, "E0.0.1062", {"start": v(-3.18, 249.33) * mm, "end": v(-3.3, 248.91) * mm});
            skLineSegment(sketch, "E0.0.1063", {"start": v(-3.3, 248.91) * mm, "end": v(-3.42, 248.5) * mm});
            skLineSegment(sketch, "E0.0.1064", {"start": v(-3.42, 248.5) * mm, "end": v(0.36, 245.94) * mm});
            skLineSegment(sketch, "E0.0.1065", {"start": v(0.36, 245.94) * mm, "end": v(0.7, 246.2) * mm});
            skLineSegment(sketch, "E0.0.1066", {"start": v(0.7, 246.2) * mm, "end": v(1.04, 246.47) * mm});
            skLineSegment(sketch, "E0.0.1067", {"start": v(1.04, 246.47) * mm, "end": v(1.74, 247) * mm});
            skLineSegment(sketch, "E0.0.1068", {"start": v(1.74, 247) * mm, "end": v(3.16, 248.01) * mm});
            skLineSegment(sketch, "E0.0.1069", {"start": v(3.16, 248.01) * mm, "end": v(4.62, 249) * mm});
            skLineSegment(sketch, "E0.0.1070", {"start": v(4.62, 249) * mm, "end": v(6.11, 249.96) * mm});
            skLineSegment(sketch, "E0.0.1071", {"start": v(6.11, 249.96) * mm, "end": v(9.67, 247.37) * mm});
            skLineSegment(sketch, "E0.0.1072", {"start": v(9.67, 247.37) * mm, "end": v(9.21, 245.65) * mm});
            skLineSegment(sketch, "E0.0.1073", {"start": v(9.21, 245.65) * mm, "end": v(8.72, 243.96) * mm});
            skLineSegment(sketch, "E0.0.1074", {"start": v(8.72, 243.96) * mm, "end": v(8.18, 242.3) * mm});
            skLineSegment(sketch, "E0.0.1075", {"start": v(8.18, 242.3) * mm, "end": v(7.9, 241.48) * mm});
            skLineSegment(sketch, "E0.0.1076", {"start": v(7.9, 241.48) * mm, "end": v(7.75, 241.07) * mm});
            skLineSegment(sketch, "E0.0.1077", {"start": v(7.75, 241.07) * mm, "end": v(7.6, 240.66) * mm});
            skLineSegment(sketch, "E0.0.1078", {"start": v(7.6, 240.66) * mm, "end": v(11.2, 237.85) * mm});
            skLineSegment(sketch, "E0.0.1079", {"start": v(11.2, 237.85) * mm, "end": v(11.55, 238.1) * mm});
            skLineSegment(sketch, "E0.0.1080", {"start": v(11.55, 238.1) * mm, "end": v(11.91, 238.33) * mm});
            skLineSegment(sketch, "E0.0.1081", {"start": v(11.91, 238.33) * mm, "end": v(12.64, 238.8) * mm});
            skLineSegment(sketch, "E0.0.1082", {"start": v(12.64, 238.8) * mm, "end": v(14.13, 239.72) * mm});
            skLineSegment(sketch, "E0.0.1083", {"start": v(14.13, 239.72) * mm, "end": v(15.65, 240.6) * mm});
            skLineSegment(sketch, "E0.0.1084", {"start": v(15.65, 240.6) * mm, "end": v(17.21, 241.46) * mm});
            skLineSegment(sketch, "E0.0.1085", {"start": v(17.21, 241.46) * mm, "end": v(20.58, 238.63) * mm});
            skLineSegment(sketch, "E0.0.1086", {"start": v(20.58, 238.63) * mm, "end": v(20, 236.95) * mm});
            skLineSegment(sketch, "E0.0.1087", {"start": v(20, 236.95) * mm, "end": v(19.4, 235.3) * mm});
            skLineSegment(sketch, "E0.0.1088", {"start": v(19.4, 235.3) * mm, "end": v(18.74, 233.67) * mm});
            skLineSegment(sketch, "E0.0.1089", {"start": v(18.74, 233.67) * mm, "end": v(18.4, 232.87) * mm});
            skLineSegment(sketch, "E0.0.1090", {"start": v(18.4, 232.87) * mm, "end": v(18.23, 232.47) * mm});
            skLineSegment(sketch, "E0.0.1091", {"start": v(18.23, 232.47) * mm, "end": v(18.05, 232.08) * mm});
            skLineSegment(sketch, "E0.0.1092", {"start": v(18.05, 232.08) * mm, "end": v(21.43, 229.02) * mm});
            skLineSegment(sketch, "E0.0.1093", {"start": v(21.43, 229.02) * mm, "end": v(21.8, 229.24) * mm});
            skLineSegment(sketch, "E0.0.1094", {"start": v(21.8, 229.24) * mm, "end": v(22.19, 229.45) * mm});
            skLineSegment(sketch, "E0.0.1095", {"start": v(22.19, 229.45) * mm, "end": v(22.95, 229.87) * mm});
            skLineSegment(sketch, "E0.0.1096", {"start": v(22.95, 229.87) * mm, "end": v(24.5, 230.68) * mm});
            skLineSegment(sketch, "E0.0.1097", {"start": v(24.5, 230.68) * mm, "end": v(26.08, 231.46) * mm});
            skLineSegment(sketch, "E0.0.1098", {"start": v(26.08, 231.46) * mm, "end": v(27.7, 232.2) * mm});
            skLineSegment(sketch, "E0.0.1099", {"start": v(27.7, 232.2) * mm, "end": v(30.85, 229.14) * mm});
            skLineSegment(sketch, "E0.0.1100", {"start": v(30.85, 229.14) * mm, "end": v(30.16, 227.5) * mm});
            skLineSegment(sketch, "E0.0.1101", {"start": v(30.16, 227.5) * mm, "end": v(29.43, 225.9) * mm});
            skLineSegment(sketch, "E0.0.1102", {"start": v(29.43, 225.9) * mm, "end": v(28.67, 224.33) * mm});
            skLineSegment(sketch, "E0.0.1103", {"start": v(28.67, 224.33) * mm, "end": v(28.28, 223.55) * mm});
            skLineSegment(sketch, "E0.0.1104", {"start": v(28.28, 223.55) * mm, "end": v(28.08, 223.17) * mm});
            skLineSegment(sketch, "E0.0.1105", {"start": v(28.08, 223.17) * mm, "end": v(27.87, 222.79) * mm});
            skLineSegment(sketch, "E0.0.1106", {"start": v(27.87, 222.79) * mm, "end": v(31.04, 219.5) * mm});
            skLineSegment(sketch, "E0.0.1107", {"start": v(31.04, 219.5) * mm, "end": v(31.42, 219.7) * mm});
            skLineSegment(sketch, "E0.0.1108", {"start": v(31.42, 219.7) * mm, "end": v(31.82, 219.88) * mm});
            skLineSegment(sketch, "E0.0.1109", {"start": v(31.82, 219.88) * mm, "end": v(32.6, 220.25) * mm});
            skLineSegment(sketch, "E0.0.1110", {"start": v(32.6, 220.25) * mm, "end": v(34.2, 220.95) * mm});
            skLineSegment(sketch, "E0.0.1111", {"start": v(34.2, 220.95) * mm, "end": v(35.84, 221.61) * mm});
            skLineSegment(sketch, "E0.0.1112", {"start": v(35.84, 221.61) * mm, "end": v(37.5, 222.24) * mm});
            skLineSegment(sketch, "E0.0.1113", {"start": v(37.5, 222.24) * mm, "end": v(40.44, 218.97) * mm});
            skLineSegment(sketch, "E0.0.1114", {"start": v(40.44, 218.97) * mm, "end": v(39.64, 217.38) * mm});
            skLineSegment(sketch, "E0.0.1115", {"start": v(39.64, 217.38) * mm, "end": v(38.8, 215.83) * mm});
            skLineSegment(sketch, "E0.0.1116", {"start": v(38.8, 215.83) * mm, "end": v(37.93, 214.32) * mm});
            skLineSegment(sketch, "E0.0.1117", {"start": v(37.93, 214.32) * mm, "end": v(37.48, 213.57) * mm});
            skLineSegment(sketch, "E0.0.1118", {"start": v(37.48, 213.57) * mm, "end": v(37.25, 213.2) * mm});
            skLineSegment(sketch, "E0.0.1119", {"start": v(37.25, 213.2) * mm, "end": v(37.02, 212.84) * mm});
            skLineSegment(sketch, "E0.0.1120", {"start": v(37.02, 212.84) * mm, "end": v(39.95, 209.34) * mm});
            skLineSegment(sketch, "E0.0.1121", {"start": v(39.95, 209.34) * mm, "end": v(40.35, 209.5) * mm});
            skLineSegment(sketch, "E0.0.1122", {"start": v(40.35, 209.5) * mm, "end": v(40.75, 209.66) * mm});
            skLineSegment(sketch, "E0.0.1123", {"start": v(40.75, 209.66) * mm, "end": v(41.56, 209.97) * mm});
            skLineSegment(sketch, "E0.0.1124", {"start": v(41.56, 209.97) * mm, "end": v(43.21, 210.56) * mm});
            skLineSegment(sketch, "E0.0.1125", {"start": v(43.21, 210.56) * mm, "end": v(44.89, 211.1) * mm});
            skLineSegment(sketch, "E0.0.1126", {"start": v(44.89, 211.1) * mm, "end": v(46.59, 211.62) * mm});
            skLineSegment(sketch, "E0.0.1127", {"start": v(46.59, 211.62) * mm, "end": v(49.3, 208.15) * mm});
            skLineSegment(sketch, "E0.0.1128", {"start": v(49.3, 208.15) * mm, "end": v(48.38, 206.62) * mm});
            skLineSegment(sketch, "E0.0.1129", {"start": v(48.38, 206.62) * mm, "end": v(47.44, 205.13) * mm});
            skLineSegment(sketch, "E0.0.1130", {"start": v(47.44, 205.13) * mm, "end": v(46.46, 203.68) * mm});
            skLineSegment(sketch, "E0.0.1131", {"start": v(46.46, 203.68) * mm, "end": v(45.96, 202.97) * mm});
            skLineSegment(sketch, "E0.0.1132", {"start": v(45.96, 202.97) * mm, "end": v(45.71, 202.62) * mm});
            skLineSegment(sketch, "E0.0.1133", {"start": v(45.71, 202.62) * mm, "end": v(45.46, 202.27) * mm});
            skLineSegment(sketch, "E0.0.1134", {"start": v(45.46, 202.27) * mm, "end": v(48.13, 198.58) * mm});
            skLineSegment(sketch, "E0.0.1135", {"start": v(48.13, 198.58) * mm, "end": v(48.54, 198.71) * mm});
            skLineSegment(sketch, "E0.0.1136", {"start": v(48.54, 198.71) * mm, "end": v(48.96, 198.84) * mm});
            skLineSegment(sketch, "E0.0.1137", {"start": v(48.96, 198.84) * mm, "end": v(49.79, 199.1) * mm});
            skLineSegment(sketch, "E0.0.1138", {"start": v(49.79, 199.1) * mm, "end": v(51.47, 199.56) * mm});
            skLineSegment(sketch, "E0.0.1139", {"start": v(51.47, 199.56) * mm, "end": v(53.18, 200) * mm});
            skLineSegment(sketch, "E0.0.1140", {"start": v(53.18, 200) * mm, "end": v(54.91, 200.39) * mm});
            skLineSegment(sketch, "E0.0.1141", {"start": v(54.91, 200.39) * mm, "end": v(57.37, 196.74) * mm});
            skLineSegment(sketch, "E0.0.1142", {"start": v(57.37, 196.74) * mm, "end": v(56.35, 195.28) * mm});
            skLineSegment(sketch, "E0.0.1143", {"start": v(56.35, 195.28) * mm, "end": v(55.3, 193.86) * mm});
            skLineSegment(sketch, "E0.0.1144", {"start": v(55.3, 193.86) * mm, "end": v(54.24, 192.48) * mm});
            skLineSegment(sketch, "E0.0.1145", {"start": v(54.24, 192.48) * mm, "end": v(53.69, 191.8) * mm});
            skLineSegment(sketch, "E0.0.1146", {"start": v(53.69, 191.8) * mm, "end": v(53.41, 191.47) * mm});
            skLineSegment(sketch, "E0.0.1147", {"start": v(53.41, 191.47) * mm, "end": v(53.13, 191.14) * mm});
            skLineSegment(sketch, "E0.0.1148", {"start": v(53.13, 191.14) * mm, "end": v(55.54, 187.27) * mm});
            skLineSegment(sketch, "E0.0.1149", {"start": v(55.54, 187.27) * mm, "end": v(55.96, 187.37) * mm});
            skLineSegment(sketch, "E0.0.1150", {"start": v(55.96, 187.37) * mm, "end": v(56.38, 187.47) * mm});
            skLineSegment(sketch, "E0.0.1151", {"start": v(56.38, 187.47) * mm, "end": v(57.23, 187.67) * mm});
            skLineSegment(sketch, "E0.0.1152", {"start": v(57.23, 187.67) * mm, "end": v(58.94, 188.02) * mm});
            skLineSegment(sketch, "E0.0.1153", {"start": v(58.94, 188.02) * mm, "end": v(60.68, 188.33) * mm});
            skLineSegment(sketch, "E0.0.1154", {"start": v(60.68, 188.33) * mm, "end": v(62.44, 188.6) * mm});
            skLineSegment(sketch, "E0.0.1155", {"start": v(62.44, 188.6) * mm, "end": v(64.63, 184.79) * mm});
            skLineSegment(sketch, "E0.0.1156", {"start": v(64.63, 184.79) * mm, "end": v(63.51, 183.4) * mm});
            skLineSegment(sketch, "E0.0.1157", {"start": v(63.51, 183.4) * mm, "end": v(62.37, 182.06) * mm});
            skLineSegment(sketch, "E0.0.1158", {"start": v(62.37, 182.06) * mm, "end": v(61.2, 180.76) * mm});
            skLineSegment(sketch, "E0.0.1159", {"start": v(61.2, 180.76) * mm, "end": v(60.61, 180.13) * mm});
            skLineSegment(sketch, "E0.0.1160", {"start": v(60.61, 180.13) * mm, "end": v(60.32, 179.81) * mm});
            skLineSegment(sketch, "E0.0.1161", {"start": v(60.32, 179.81) * mm, "end": v(60.02, 179.5) * mm});
            skLineSegment(sketch, "E0.0.1162", {"start": v(60.02, 179.5) * mm, "end": v(62.15, 175.47) * mm});
            skLineSegment(sketch, "E0.0.1163", {"start": v(62.15, 175.47) * mm, "end": v(62.58, 175.55) * mm});
            skLineSegment(sketch, "E0.0.1164", {"start": v(62.58, 175.55) * mm, "end": v(63, 175.62) * mm});
            skLineSegment(sketch, "E0.0.1165", {"start": v(63, 175.62) * mm, "end": v(63.86, 175.75) * mm});
            skLineSegment(sketch, "E0.0.1166", {"start": v(63.86, 175.75) * mm, "end": v(65.6, 175.99) * mm});
            skLineSegment(sketch, "E0.0.1167", {"start": v(65.6, 175.99) * mm, "end": v(67.35, 176.18) * mm});
            skLineSegment(sketch, "E0.0.1168", {"start": v(67.35, 176.18) * mm, "end": v(69.12, 176.32) * mm});
            skLineSegment(sketch, "E0.0.1169", {"start": v(69.12, 176.32) * mm, "end": v(71.04, 172.36) * mm});
            skLineSegment(sketch, "E0.0.1170", {"start": v(71.04, 172.36) * mm, "end": v(69.83, 171.06) * mm});
            skLineSegment(sketch, "E0.0.1171", {"start": v(69.83, 171.06) * mm, "end": v(68.6, 169.8) * mm});
            skLineSegment(sketch, "E0.0.1172", {"start": v(68.6, 169.8) * mm, "end": v(67.34, 168.58) * mm});
            skLineSegment(sketch, "E0.0.1173", {"start": v(67.34, 168.58) * mm, "end": v(66.7, 168) * mm});
            skLineSegment(sketch, "E0.0.1174", {"start": v(66.7, 168) * mm, "end": v(66.39, 167.7) * mm});
            skLineSegment(sketch, "E0.0.1175", {"start": v(66.39, 167.7) * mm, "end": v(66.07, 167.41) * mm});
            skLineSegment(sketch, "E0.0.1176", {"start": v(66.07, 167.41) * mm, "end": v(67.92, 163.24) * mm});
            skLineSegment(sketch, "E0.0.1177", {"start": v(67.92, 163.24) * mm, "end": v(68.35, 163.29) * mm});
            skLineSegment(sketch, "E0.0.1178", {"start": v(68.35, 163.29) * mm, "end": v(68.78, 163.33) * mm});
            skLineSegment(sketch, "E0.0.1179", {"start": v(68.78, 163.33) * mm, "end": v(69.64, 163.4) * mm});
            skLineSegment(sketch, "E0.0.1180", {"start": v(69.64, 163.4) * mm, "end": v(71.39, 163.52) * mm});
            skLineSegment(sketch, "E0.0.1181", {"start": v(71.39, 163.52) * mm, "end": v(73.15, 163.58) * mm});
            skLineSegment(sketch, "E0.0.1182", {"start": v(73.15, 163.58) * mm, "end": v(74.93, 163.6) * mm});
            skLineSegment(sketch, "E0.0.1183", {"start": v(74.93, 163.6) * mm, "end": v(76.57, 159.52) * mm});
            skLineSegment(sketch, "E0.0.1184", {"start": v(76.57, 159.52) * mm, "end": v(75.27, 158.3) * mm});
            skLineSegment(sketch, "E0.0.1185", {"start": v(75.27, 158.3) * mm, "end": v(73.95, 157.14) * mm});
            skLineSegment(sketch, "E0.0.1186", {"start": v(73.95, 157.14) * mm, "end": v(72.62, 156) * mm});
            skLineSegment(sketch, "E0.0.1187", {"start": v(72.62, 156) * mm, "end": v(71.94, 155.46) * mm});
            skLineSegment(sketch, "E0.0.1188", {"start": v(71.94, 155.46) * mm, "end": v(71.6, 155.2) * mm});
            skLineSegment(sketch, "E0.0.1189", {"start": v(71.6, 155.2) * mm, "end": v(71.26, 154.93) * mm});
            skLineSegment(sketch, "E0.0.1190", {"start": v(71.26, 154.93) * mm, "end": v(72.82, 150.64) * mm});
            skLineSegment(sketch, "E0.0.1191", {"start": v(72.82, 150.64) * mm, "end": v(73.25, 150.66) * mm});
            skLineSegment(sketch, "E0.0.1192", {"start": v(73.25, 150.66) * mm, "end": v(73.68, 150.67) * mm});
            skLineSegment(sketch, "E0.0.1193", {"start": v(73.68, 150.67) * mm, "end": v(74.55, 150.68) * mm});
            skLineSegment(sketch, "E0.0.1194", {"start": v(74.55, 150.68) * mm, "end": v(76.3, 150.67) * mm});
            skLineSegment(sketch, "E0.0.1195", {"start": v(76.3, 150.67) * mm, "end": v(78.06, 150.62) * mm});
            skLineSegment(sketch, "E0.0.1196", {"start": v(78.06, 150.62) * mm, "end": v(79.83, 150.52) * mm});
            skLineSegment(sketch, "E0.0.1197", {"start": v(79.83, 150.52) * mm, "end": v(81.19, 146.33) * mm});
            skLineSegment(sketch, "E0.0.1198", {"start": v(81.19, 146.33) * mm, "end": v(79.8, 145.2) * mm});
            skLineSegment(sketch, "E0.0.1199", {"start": v(79.8, 145.2) * mm, "end": v(78.41, 144.13) * mm});
            skLineSegment(sketch, "E0.0.1200", {"start": v(78.41, 144.13) * mm, "end": v(77, 143.1) * mm});
            skLineSegment(sketch, "E0.0.1201", {"start": v(77, 143.1) * mm, "end": v(76.29, 142.6) * mm});
            skLineSegment(sketch, "E0.0.1202", {"start": v(76.29, 142.6) * mm, "end": v(75.93, 142.36) * mm});
            skLineSegment(sketch, "E0.0.1203", {"start": v(75.93, 142.36) * mm, "end": v(75.57, 142.11) * mm});
            skLineSegment(sketch, "E0.0.1204", {"start": v(75.57, 142.11) * mm, "end": v(76.82, 137.73) * mm});
            skLineSegment(sketch, "E0.0.1205", {"start": v(76.82, 137.73) * mm, "end": v(77.26, 137.72) * mm});
            skLineSegment(sketch, "E0.0.1206", {"start": v(77.26, 137.72) * mm, "end": v(77.69, 137.7) * mm});
            skLineSegment(sketch, "E0.0.1207", {"start": v(77.69, 137.7) * mm, "end": v(78.56, 137.65) * mm});
            skLineSegment(sketch, "E0.0.1208", {"start": v(78.56, 137.65) * mm, "end": v(80.3, 137.52) * mm});
            skLineSegment(sketch, "E0.0.1209", {"start": v(80.3, 137.52) * mm, "end": v(82.05, 137.34) * mm});
            skLineSegment(sketch, "E0.0.1210", {"start": v(82.05, 137.34) * mm, "end": v(83.82, 137.12) * mm});
            skLineSegment(sketch, "E0.0.1211", {"start": v(83.82, 137.12) * mm, "end": v(84.87, 132.84) * mm});
            skLineSegment(sketch, "E0.0.1212", {"start": v(84.87, 132.84) * mm, "end": v(83.42, 131.82) * mm});
            skLineSegment(sketch, "E0.0.1213", {"start": v(83.42, 131.82) * mm, "end": v(81.95, 130.84) * mm});
            skLineSegment(sketch, "E0.0.1214", {"start": v(81.95, 130.84) * mm, "end": v(80.47, 129.91) * mm});
            skLineSegment(sketch, "E0.0.1215", {"start": v(80.47, 129.91) * mm, "end": v(79.73, 129.47) * mm});
            skLineSegment(sketch, "E0.0.1216", {"start": v(79.73, 129.47) * mm, "end": v(79.35, 129.25) * mm});
            skLineSegment(sketch, "E0.0.1217", {"start": v(79.35, 129.25) * mm, "end": v(78.98, 129.03) * mm});
            skLineSegment(sketch, "E0.0.1218", {"start": v(78.98, 129.03) * mm, "end": v(79.92, 124.57) * mm});
            skLineSegment(sketch, "E0.0.1219", {"start": v(79.92, 124.57) * mm, "end": v(80.35, 124.52) * mm});
            skLineSegment(sketch, "E0.0.1220", {"start": v(80.35, 124.52) * mm, "end": v(80.78, 124.48) * mm});
            skLineSegment(sketch, "E0.0.1221", {"start": v(80.78, 124.48) * mm, "end": v(81.64, 124.37) * mm});
            skLineSegment(sketch, "E0.0.1222", {"start": v(81.64, 124.37) * mm, "end": v(83.37, 124.11) * mm});
            skLineSegment(sketch, "E0.0.1223", {"start": v(83.37, 124.11) * mm, "end": v(85.1, 123.81) * mm});
            skLineSegment(sketch, "E0.0.1224", {"start": v(85.1, 123.81) * mm, "end": v(86.85, 123.47) * mm});
            skLineSegment(sketch, "E0.0.1225", {"start": v(86.85, 123.47) * mm, "end": v(87.61, 119.13) * mm});
            skLineSegment(sketch, "E0.0.1226", {"start": v(87.61, 119.13) * mm, "end": v(86.09, 118.21) * mm});
            skLineSegment(sketch, "E0.0.1227", {"start": v(86.09, 118.21) * mm, "end": v(84.56, 117.34) * mm});
            skLineSegment(sketch, "E0.0.1228", {"start": v(84.56, 117.34) * mm, "end": v(83.02, 116.52) * mm});
            skLineSegment(sketch, "E0.0.1229", {"start": v(83.02, 116.52) * mm, "end": v(82.24, 116.12) * mm});
            skLineSegment(sketch, "E0.0.1230", {"start": v(82.24, 116.12) * mm, "end": v(81.85, 115.93) * mm});
            skLineSegment(sketch, "E0.0.1231", {"start": v(81.85, 115.93) * mm, "end": v(81.47, 115.74) * mm});
            skLineSegment(sketch, "E0.0.1232", {"start": v(81.47, 115.74) * mm, "end": v(82.1, 111.23) * mm});
            skLineSegment(sketch, "E0.0.1233", {"start": v(82.1, 111.23) * mm, "end": v(82.52, 111.15) * mm});
            skLineSegment(sketch, "E0.0.1234", {"start": v(82.52, 111.15) * mm, "end": v(82.94, 111.07) * mm});
            skLineSegment(sketch, "E0.0.1235", {"start": v(82.94, 111.07) * mm, "end": v(83.8, 110.9) * mm});
            skLineSegment(sketch, "E0.0.1236", {"start": v(83.8, 110.9) * mm, "end": v(85.5, 110.53) * mm});
            skLineSegment(sketch, "E0.0.1237", {"start": v(85.5, 110.53) * mm, "end": v(87.22, 110.1) * mm});
            skLineSegment(sketch, "E0.0.1238", {"start": v(87.22, 110.1) * mm, "end": v(88.93, 109.64) * mm});
            skLineSegment(sketch, "E0.0.1239", {"start": v(88.93, 109.64) * mm, "end": v(89.39, 105.26) * mm});
            skLineSegment(sketch, "E0.0.1240", {"start": v(89.39, 105.26) * mm, "end": v(87.8, 104.45) * mm});
            skLineSegment(sketch, "E0.0.1241", {"start": v(87.8, 104.45) * mm, "end": v(86.21, 103.7) * mm});
            skLineSegment(sketch, "E0.0.1242", {"start": v(86.21, 103.7) * mm, "end": v(84.62, 102.98) * mm});
            skLineSegment(sketch, "E0.0.1243", {"start": v(84.62, 102.98) * mm, "end": v(83.82, 102.64) * mm});
            skLineSegment(sketch, "E0.0.1244", {"start": v(83.82, 102.64) * mm, "end": v(83.42, 102.47) * mm});
            skLineSegment(sketch, "E0.0.1245", {"start": v(83.42, 102.47) * mm, "end": v(83.02, 102.31) * mm});
            skLineSegment(sketch, "E0.0.1246", {"start": v(83.02, 102.31) * mm, "end": v(83.33, 97.76) * mm});
            skLineSegment(sketch, "E0.0.1247", {"start": v(83.33, 97.76) * mm, "end": v(83.75, 97.66) * mm});
            skLineSegment(sketch, "E0.0.1248", {"start": v(83.75, 97.66) * mm, "end": v(84.17, 97.55) * mm});
            skLineSegment(sketch, "E0.0.1249", {"start": v(84.17, 97.55) * mm, "end": v(85, 97.32) * mm});
            skLineSegment(sketch, "E0.0.1250", {"start": v(85, 97.32) * mm, "end": v(86.68, 96.83) * mm});
            skLineSegment(sketch, "E0.0.1251", {"start": v(86.68, 96.83) * mm, "end": v(88.36, 96.3) * mm});
            skLineSegment(sketch, "E0.0.1252", {"start": v(88.36, 96.3) * mm, "end": v(90.04, 95.7) * mm});
            skLineSegment(sketch, "E0.0.1253", {"start": v(90.04, 95.7) * mm, "end": v(90.19, 91.3) * mm});
            skLineSegment(sketch, "E0.0.1254", {"start": v(90.19, 91.3) * mm, "end": v(88.55, 90.6) * mm});
            skLineSegment(sketch, "E0.0.1255", {"start": v(88.55, 90.6) * mm, "end": v(86.91, 89.96) * mm});
            skLineSegment(sketch, "E0.0.1256", {"start": v(86.91, 89.96) * mm, "end": v(85.27, 89.36) * mm});
            skLineSegment(sketch, "E0.0.1257", {"start": v(85.27, 89.36) * mm, "end": v(84.45, 89.07) * mm});
            skLineSegment(sketch, "E0.0.1258", {"start": v(84.45, 89.07) * mm, "end": v(84.04, 88.94) * mm});
            skLineSegment(sketch, "E0.0.1259", {"start": v(84.04, 88.94) * mm, "end": v(83.63, 88.8) * mm});
            skCircle(sketch, "E1", {"center": v(-110.06, 86.8) * mm, "radius": 5 * mm});
            skSolve(sketch);
        }
        {
            var Q0;
            Q0=makeQuery(id+"F0.imprint","IMPRINT",FACE,{"disambiguationData":[TD([[makeQuery(id+"F0.imprint","IMPRINT",EDGE,{"derivedFrom":sQuery(id+"F0.wireOp",EDGE,"E0.0.0")}),-1.0]])]});
            extrude(context, id + "F1", {"entities" : qUnion([Q0]), "depth" : 9 * mm, "offsetDistance" : 25 * mm});
        }
    });
